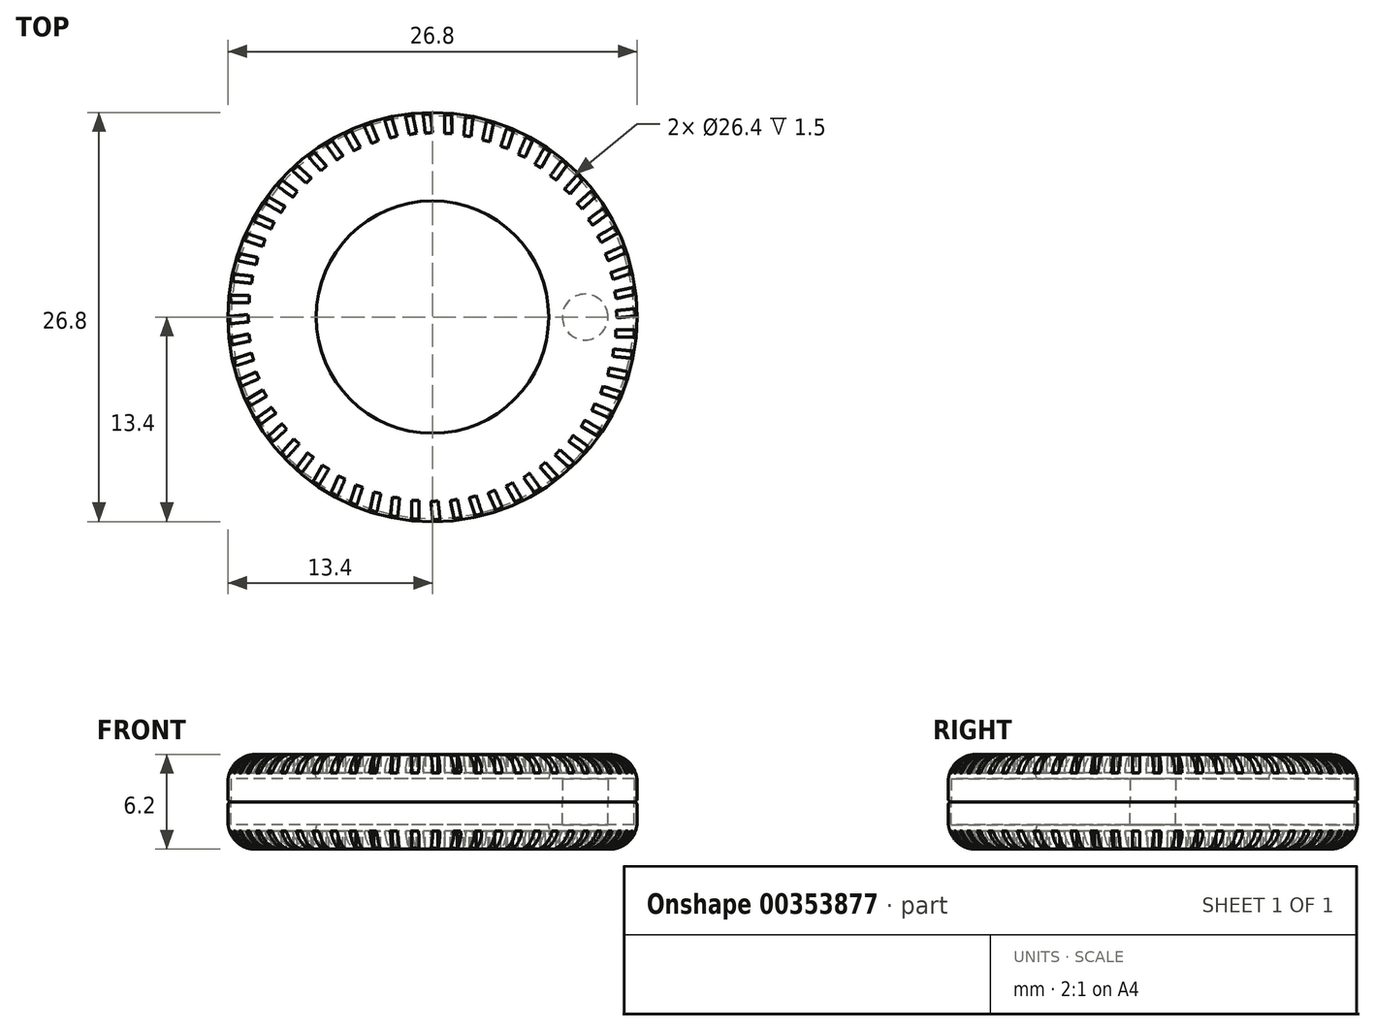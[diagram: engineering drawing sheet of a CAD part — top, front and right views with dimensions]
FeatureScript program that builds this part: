
annotation { "Feature Type Name" : "Feature", "Feature Type Description" : "" }
export const myFeature = defineFeature(function(context is Context, id is Id, definition is map)
    precondition{}
    {
        {
            var Q0;
            Q0=qCreatedBy(makeId("Top.planeOp"),FACE);
            var sketch = newSketch(context, id + "F0", { "sketchPlane" : qUnion([Q0])});
            skCircle(sketch, "E0", {"center": v(0, 0) * mm, "radius": 13.4 * mm});
            skCircle(sketch, "E1", {"center": v(0, 0) * mm, "radius": 7.6 * mm});
            skSolve(sketch);
        }
        {
            var Q0;
            Q0=makeQuery(id+"F0.imprint","IMPRINT",FACE,{"disambiguationData":[TD([[makeQuery(id+"F0.imprint","IMPRINT",EDGE,{"derivedFrom":sQuery(id+"F0.wireOp",EDGE,"E0")}),1.0]])]});
            extrude(context, id + "F1", {"entities" : qUnion([Q0]), "depth" : 3.1 * mm});
        }
        {
            var Q0;
            Q0=makeQuery(id+"F1.opExtrude","CAP_EDGE",EDGE,{"disambiguationData":[OSD([sQuery(id+"F0.wireOp",EDGE,"E0")])],"isStart":true});
            fillet(context, id + "F2", {"entities" : qUnion([Q0]), "radius" : .2 * mm, "tangentPropagation" : true, "allowEdgeOverflow" : false});
        }
        {
            var Q0;
            Q0=makeQuery(id+"F1.opExtrude","CAP_EDGE",EDGE,{"disambiguationData":[OSD([sQuery(id+"F0.wireOp",EDGE,"E0")])],"isStart":false});
            var Q1;
            Q1=makeQuery(id+"F1.opExtrude","CAP_EDGE",EDGE,{"disambiguationData":[OSD([sQuery(id+"F0.wireOp",EDGE,"E1")])],"isStart":false});
            fillet(context, id + "F3", {"entities" : qUnion([Q0, Q1]), "radius" : 1.8 * mm, "tangentPropagation" : true, "allowEdgeOverflow" : false});
        }
        {
            var Q0;
            Q0=qCreatedBy(makeId("Top.planeOp"),FACE);
            var sketch = newSketch(context, id + "F4", { "sketchPlane" : qUnion([Q0])});
            skLineSegment(sketch, "E2", {"start": v(0, 13.73) * mm, "end": v(-0.13, 13.18) * mm});
            skLineSegment(sketch, "E3", {"start": v(-0.13, 13.18) * mm, "end": v(0, 12.1) * mm});
            skLineSegment(sketch, "E4", {"start": v(0, 12.1) * mm, "end": v(-0.47, 12.04) * mm});
            skLineSegment(sketch, "E5", {"start": v(-0.47, 12.04) * mm, "end": v(-0.6, 13.18) * mm});
            skLineSegment(sketch, "E6", {"start": v(-0.6, 13.18) * mm, "end": v(-0.48, 13.73) * mm});
            skLineSegment(sketch, "E7", {"start": v(-0.48, 13.73) * mm, "end": v(0, 13.73) * mm});
            skLineSegment(sketch, "E8.1.0", {"start": v(1.26, 13.12) * mm, "end": v(1.27, 12.02) * mm});
            skLineSegment(sketch, "E8.1.1", {"start": v(1.44, 13.65) * mm, "end": v(1.26, 13.12) * mm});
            skLineSegment(sketch, "E8.1.2", {"start": v(0.8, 12.02) * mm, "end": v(0.78, 13.17) * mm});
            skLineSegment(sketch, "E8.1.3", {"start": v(0.78, 13.17) * mm, "end": v(0.96, 13.7) * mm});
            skLineSegment(sketch, "E8.1.4", {"start": v(1.27, 12.02) * mm, "end": v(0.8, 12.02) * mm});
            skLineSegment(sketch, "E8.1.5", {"start": v(0.96, 13.7) * mm, "end": v(1.44, 13.65) * mm});
            skLineSegment(sketch, "E8.2.0", {"start": v(2.63, 12.92) * mm, "end": v(2.52, 11.82) * mm});
            skLineSegment(sketch, "E8.2.1", {"start": v(2.86, 13.43) * mm, "end": v(2.63, 12.92) * mm});
            skLineSegment(sketch, "E8.2.2", {"start": v(2.05, 11.87) * mm, "end": v(2.16, 13.02) * mm});
            skLineSegment(sketch, "E8.2.3", {"start": v(2.16, 13.02) * mm, "end": v(2.4, 13.53) * mm});
            skLineSegment(sketch, "E8.2.4", {"start": v(2.52, 11.82) * mm, "end": v(2.05, 11.87) * mm});
            skLineSegment(sketch, "E8.2.5", {"start": v(2.4, 13.53) * mm, "end": v(2.86, 13.43) * mm});
            skLineSegment(sketch, "E8.3.0", {"start": v(3.96, 12.57) * mm, "end": v(3.75, 11.5) * mm});
            skLineSegment(sketch, "E8.3.1", {"start": v(4.25, 13.05) * mm, "end": v(3.96, 12.57) * mm});
            skLineSegment(sketch, "E8.3.2", {"start": v(3.28, 11.6) * mm, "end": v(3.51, 12.72) * mm});
            skLineSegment(sketch, "E8.3.3", {"start": v(3.51, 12.72) * mm, "end": v(3.8, 13.2) * mm});
            skLineSegment(sketch, "E8.3.4", {"start": v(3.75, 11.5) * mm, "end": v(3.28, 11.6) * mm});
            skLineSegment(sketch, "E8.3.5", {"start": v(3.8, 13.2) * mm, "end": v(4.25, 13.05) * mm});
            skLineSegment(sketch, "E8.4.0", {"start": v(5.26, 12.08) * mm, "end": v(4.93, 11.04) * mm});
            skLineSegment(sketch, "E8.4.1", {"start": v(5.6, 12.54) * mm, "end": v(5.26, 12.08) * mm});
            skLineSegment(sketch, "E8.4.2", {"start": v(4.48, 11.18) * mm, "end": v(4.82, 12.28) * mm});
            skLineSegment(sketch, "E8.4.3", {"start": v(4.82, 12.28) * mm, "end": v(5.16, 12.73) * mm});
            skLineSegment(sketch, "E8.4.4", {"start": v(4.93, 11.04) * mm, "end": v(4.48, 11.18) * mm});
            skLineSegment(sketch, "E8.4.5", {"start": v(5.16, 12.73) * mm, "end": v(5.6, 12.54) * mm});
            skLineSegment(sketch, "E8.5.0", {"start": v(6.5, 11.47) * mm, "end": v(6.06, 10.46) * mm});
            skLineSegment(sketch, "E8.5.1", {"start": v(6.88, 11.88) * mm, "end": v(6.5, 11.47) * mm});
            skLineSegment(sketch, "E8.5.2", {"start": v(5.63, 10.65) * mm, "end": v(6.08, 11.7) * mm});
            skLineSegment(sketch, "E8.5.3", {"start": v(6.08, 11.7) * mm, "end": v(6.47, 12.12) * mm});
            skLineSegment(sketch, "E8.5.4", {"start": v(6.06, 10.46) * mm, "end": v(5.63, 10.65) * mm});
            skLineSegment(sketch, "E8.5.5", {"start": v(6.47, 12.12) * mm, "end": v(6.88, 11.88) * mm});
            skLineSegment(sketch, "E8.6.0", {"start": v(7.66, 10.72) * mm, "end": v(7.12, 9.77) * mm});
            skLineSegment(sketch, "E8.6.1", {"start": v(8.09, 11.1) * mm, "end": v(7.66, 10.72) * mm});
            skLineSegment(sketch, "E8.6.2", {"start": v(6.71, 10) * mm, "end": v(7.28, 11) * mm});
            skLineSegment(sketch, "E8.6.3", {"start": v(7.28, 11) * mm, "end": v(7.7, 11.37) * mm});
            skLineSegment(sketch, "E8.6.4", {"start": v(7.12, 9.77) * mm, "end": v(6.71, 10) * mm});
            skLineSegment(sketch, "E8.6.5", {"start": v(7.7, 11.37) * mm, "end": v(8.09, 11.1) * mm});
            skLineSegment(sketch, "E8.7.0", {"start": v(8.75, 9.86) * mm, "end": v(8.1, 8.97) * mm});
            skLineSegment(sketch, "E8.7.1", {"start": v(9.2, 10.18) * mm, "end": v(8.75, 9.86) * mm});
            skLineSegment(sketch, "E8.7.2", {"start": v(7.72, 9.24) * mm, "end": v(8.4, 10.18) * mm});
            skLineSegment(sketch, "E8.7.3", {"start": v(8.4, 10.18) * mm, "end": v(8.85, 10.5) * mm});
            skLineSegment(sketch, "E8.7.4", {"start": v(8.1, 8.97) * mm, "end": v(7.72, 9.24) * mm});
            skLineSegment(sketch, "E8.7.5", {"start": v(8.85, 10.5) * mm, "end": v(9.2, 10.18) * mm});
            skLineSegment(sketch, "E8.8.0", {"start": v(9.73, 8.89) * mm, "end": v(9, 8.07) * mm});
            skLineSegment(sketch, "E8.8.1", {"start": v(10.22, 9.16) * mm, "end": v(9.73, 8.89) * mm});
            skLineSegment(sketch, "E8.8.2", {"start": v(8.65, 8.38) * mm, "end": v(9.41, 9.24) * mm});
            skLineSegment(sketch, "E8.8.3", {"start": v(9.41, 9.24) * mm, "end": v(9.9, 9.52) * mm});
            skLineSegment(sketch, "E8.8.4", {"start": v(9, 8.07) * mm, "end": v(8.65, 8.38) * mm});
            skLineSegment(sketch, "E8.8.5", {"start": v(9.9, 9.52) * mm, "end": v(10.22, 9.16) * mm});
            skLineSegment(sketch, "E8.9.0", {"start": v(10.6, 7.82) * mm, "end": v(9.8, 7.08) * mm});
            skLineSegment(sketch, "E8.9.1", {"start": v(11.13, 8.04) * mm, "end": v(10.6, 7.82) * mm});
            skLineSegment(sketch, "E8.9.2", {"start": v(9.48, 7.43) * mm, "end": v(10.33, 8.2) * mm});
            skLineSegment(sketch, "E8.9.3", {"start": v(10.33, 8.2) * mm, "end": v(10.85, 8.43) * mm});
            skLineSegment(sketch, "E8.9.4", {"start": v(9.8, 7.08) * mm, "end": v(9.48, 7.43) * mm});
            skLineSegment(sketch, "E8.9.5", {"start": v(10.85, 8.43) * mm, "end": v(11.13, 8.04) * mm});
            skLineSegment(sketch, "E8.10.0", {"start": v(11.37, 6.66) * mm, "end": v(10.49, 6.01) * mm});
            skLineSegment(sketch, "E8.10.1", {"start": v(11.91, 6.83) * mm, "end": v(11.37, 6.66) * mm});
            skLineSegment(sketch, "E8.10.2", {"start": v(10.2, 6.4) * mm, "end": v(11.13, 7.08) * mm});
            skLineSegment(sketch, "E8.10.3", {"start": v(11.13, 7.08) * mm, "end": v(11.67, 7.24) * mm});
            skLineSegment(sketch, "E8.10.4", {"start": v(10.49, 6.01) * mm, "end": v(10.2, 6.4) * mm});
            skLineSegment(sketch, "E8.10.5", {"start": v(11.67, 7.24) * mm, "end": v(11.91, 6.83) * mm});
            skLineSegment(sketch, "E8.11.0", {"start": v(12, 5.44) * mm, "end": v(11.06, 4.88) * mm});
            skLineSegment(sketch, "E8.11.1", {"start": v(12.56, 5.54) * mm, "end": v(12, 5.44) * mm});
            skLineSegment(sketch, "E8.11.2", {"start": v(10.82, 5.3) * mm, "end": v(11.81, 5.87) * mm});
            skLineSegment(sketch, "E8.11.3", {"start": v(11.81, 5.87) * mm, "end": v(12.37, 5.98) * mm});
            skLineSegment(sketch, "E8.11.4", {"start": v(11.06, 4.88) * mm, "end": v(10.82, 5.3) * mm});
            skLineSegment(sketch, "E8.11.5", {"start": v(12.37, 5.98) * mm, "end": v(12.56, 5.54) * mm});
            skLineSegment(sketch, "E8.12.0", {"start": v(12.51, 4.15) * mm, "end": v(11.51, 3.7) * mm});
            skLineSegment(sketch, "E8.12.1", {"start": v(13.07, 4.2) * mm, "end": v(12.51, 4.15) * mm});
            skLineSegment(sketch, "E8.12.2", {"start": v(11.32, 4.13) * mm, "end": v(12.36, 4.6) * mm});
            skLineSegment(sketch, "E8.12.3", {"start": v(12.36, 4.6) * mm, "end": v(12.93, 4.65) * mm});
            skLineSegment(sketch, "E8.12.4", {"start": v(11.51, 3.7) * mm, "end": v(11.32, 4.13) * mm});
            skLineSegment(sketch, "E8.12.5", {"start": v(12.93, 4.65) * mm, "end": v(13.07, 4.2) * mm});
            skLineSegment(sketch, "E8.13.0", {"start": v(12.88, 2.81) * mm, "end": v(11.84, 2.47) * mm});
            skLineSegment(sketch, "E8.13.1", {"start": v(13.44, 2.8) * mm, "end": v(12.88, 2.81) * mm});
            skLineSegment(sketch, "E8.13.2", {"start": v(11.69, 2.92) * mm, "end": v(12.78, 3.28) * mm});
            skLineSegment(sketch, "E8.13.3", {"start": v(12.78, 3.28) * mm, "end": v(13.34, 3.27) * mm});
            skLineSegment(sketch, "E8.13.4", {"start": v(11.84, 2.47) * mm, "end": v(11.69, 2.92) * mm});
            skLineSegment(sketch, "E8.13.5", {"start": v(13.34, 3.27) * mm, "end": v(13.44, 2.8) * mm});
            skLineSegment(sketch, "E8.14.0", {"start": v(13.1, 1.45) * mm, "end": v(12.03, 1.21) * mm});
            skLineSegment(sketch, "E8.14.1", {"start": v(13.66, 1.38) * mm, "end": v(13.1, 1.45) * mm});
            skLineSegment(sketch, "E8.14.2", {"start": v(11.93, 1.68) * mm, "end": v(13.05, 1.92) * mm});
            skLineSegment(sketch, "E8.14.3", {"start": v(13.05, 1.92) * mm, "end": v(13.61, 1.85) * mm});
            skLineSegment(sketch, "E8.14.4", {"start": v(12.03, 1.21) * mm, "end": v(11.93, 1.68) * mm});
            skLineSegment(sketch, "E8.14.5", {"start": v(13.61, 1.85) * mm, "end": v(13.66, 1.38) * mm});
            skLineSegment(sketch, "E8.15.0", {"start": v(13.18, 0.07) * mm, "end": v(12.1, -0.05) * mm});
            skLineSegment(sketch, "E8.15.1", {"start": v(13.73, -0.06) * mm, "end": v(13.18, 0.07) * mm});
            skLineSegment(sketch, "E8.15.2", {"start": v(12.04, 0.42) * mm, "end": v(13.18, 0.54) * mm});
            skLineSegment(sketch, "E8.15.3", {"start": v(13.18, 0.54) * mm, "end": v(13.73, 0.42) * mm});
            skLineSegment(sketch, "E8.15.4", {"start": v(12.1, -0.05) * mm, "end": v(12.04, 0.42) * mm});
            skLineSegment(sketch, "E8.15.5", {"start": v(13.73, 0.42) * mm, "end": v(13.73, -0.06) * mm});
            skLineSegment(sketch, "E8.16.0", {"start": v(13.11, -1.32) * mm, "end": v(12.02, -1.32) * mm});
            skLineSegment(sketch, "E8.16.1", {"start": v(13.65, -1.5) * mm, "end": v(13.11, -1.32) * mm});
            skLineSegment(sketch, "E8.16.2", {"start": v(12.02, -0.85) * mm, "end": v(13.17, -0.84) * mm});
            skLineSegment(sketch, "E8.16.3", {"start": v(13.17, -0.84) * mm, "end": v(13.7, -1.02) * mm});
            skLineSegment(sketch, "E8.16.4", {"start": v(12.02, -1.32) * mm, "end": v(12.02, -0.85) * mm});
            skLineSegment(sketch, "E8.16.5", {"start": v(13.7, -1.02) * mm, "end": v(13.65, -1.5) * mm});
            skLineSegment(sketch, "E8.17.0", {"start": v(12.9, -2.68) * mm, "end": v(11.81, -2.57) * mm});
            skLineSegment(sketch, "E8.17.1", {"start": v(13.41, -2.92) * mm, "end": v(12.9, -2.68) * mm});
            skLineSegment(sketch, "E8.17.2", {"start": v(11.86, -2.1) * mm, "end": v(13, -2.22) * mm});
            skLineSegment(sketch, "E8.17.3", {"start": v(13, -2.22) * mm, "end": v(13.52, -2.46) * mm});
            skLineSegment(sketch, "E8.17.4", {"start": v(11.81, -2.57) * mm, "end": v(11.86, -2.1) * mm});
            skLineSegment(sketch, "E8.17.5", {"start": v(13.52, -2.46) * mm, "end": v(13.41, -2.92) * mm});
            skLineSegment(sketch, "E8.18.0", {"start": v(12.55, -4.02) * mm, "end": v(11.48, -3.8) * mm});
            skLineSegment(sketch, "E8.18.1", {"start": v(13.03, -4.31) * mm, "end": v(12.55, -4.02) * mm});
            skLineSegment(sketch, "E8.18.2", {"start": v(11.58, -3.33) * mm, "end": v(12.7, -3.57) * mm});
            skLineSegment(sketch, "E8.18.3", {"start": v(12.7, -3.57) * mm, "end": v(13.18, -3.86) * mm});
            skLineSegment(sketch, "E8.18.4", {"start": v(11.48, -3.8) * mm, "end": v(11.58, -3.33) * mm});
            skLineSegment(sketch, "E8.18.5", {"start": v(13.18, -3.86) * mm, "end": v(13.03, -4.31) * mm});
            skLineSegment(sketch, "E8.19.0", {"start": v(12.06, -5.31) * mm, "end": v(11.02, -4.98) * mm});
            skLineSegment(sketch, "E8.19.1", {"start": v(12.51, -5.65) * mm, "end": v(12.06, -5.31) * mm});
            skLineSegment(sketch, "E8.19.2", {"start": v(11.16, -4.53) * mm, "end": v(12.26, -4.88) * mm});
            skLineSegment(sketch, "E8.19.3", {"start": v(12.26, -4.88) * mm, "end": v(12.7, -5.22) * mm});
            skLineSegment(sketch, "E8.19.4", {"start": v(11.02, -4.98) * mm, "end": v(11.16, -4.53) * mm});
            skLineSegment(sketch, "E8.19.5", {"start": v(12.7, -5.22) * mm, "end": v(12.51, -5.65) * mm});
            skLineSegment(sketch, "E8.20.0", {"start": v(11.44, -6.55) * mm, "end": v(10.43, -6.1) * mm});
            skLineSegment(sketch, "E8.20.1", {"start": v(11.85, -6.93) * mm, "end": v(11.44, -6.55) * mm});
            skLineSegment(sketch, "E8.20.2", {"start": v(10.63, -5.67) * mm, "end": v(11.68, -6.14) * mm});
            skLineSegment(sketch, "E8.20.3", {"start": v(11.68, -6.14) * mm, "end": v(12.1, -6.52) * mm});
            skLineSegment(sketch, "E8.20.4", {"start": v(10.43, -6.1) * mm, "end": v(10.63, -5.67) * mm});
            skLineSegment(sketch, "E8.20.5", {"start": v(12.1, -6.52) * mm, "end": v(11.85, -6.93) * mm});
            skLineSegment(sketch, "E8.21.0", {"start": v(10.69, -7.71) * mm, "end": v(9.74, -7.17) * mm});
            skLineSegment(sketch, "E8.21.1", {"start": v(11.06, -8.14) * mm, "end": v(10.69, -7.71) * mm});
            skLineSegment(sketch, "E8.21.2", {"start": v(9.97, -6.76) * mm, "end": v(10.97, -7.33) * mm});
            skLineSegment(sketch, "E8.21.3", {"start": v(10.97, -7.33) * mm, "end": v(11.34, -7.75) * mm});
            skLineSegment(sketch, "E8.21.4", {"start": v(9.74, -7.17) * mm, "end": v(9.97, -6.76) * mm});
            skLineSegment(sketch, "E8.21.5", {"start": v(11.34, -7.75) * mm, "end": v(11.06, -8.14) * mm});
            skLineSegment(sketch, "E8.22.0", {"start": v(9.82, -8.79) * mm, "end": v(8.93, -8.15) * mm});
            skLineSegment(sketch, "E8.22.1", {"start": v(10.14, -9.25) * mm, "end": v(9.82, -8.79) * mm});
            skLineSegment(sketch, "E8.22.2", {"start": v(9.2, -7.76) * mm, "end": v(10.14, -8.44) * mm});
            skLineSegment(sketch, "E8.22.3", {"start": v(10.14, -8.44) * mm, "end": v(10.46, -8.9) * mm});
            skLineSegment(sketch, "E8.22.4", {"start": v(8.93, -8.15) * mm, "end": v(9.2, -7.76) * mm});
            skLineSegment(sketch, "E8.22.5", {"start": v(10.46, -8.9) * mm, "end": v(10.14, -9.25) * mm});
            skLineSegment(sketch, "E8.23.0", {"start": v(8.85, -9.77) * mm, "end": v(8.03, -9.04) * mm});
            skLineSegment(sketch, "E8.23.1", {"start": v(9.12, -10.27) * mm, "end": v(8.85, -9.77) * mm});
            skLineSegment(sketch, "E8.23.2", {"start": v(8.35, -8.69) * mm, "end": v(9.2, -9.45) * mm});
            skLineSegment(sketch, "E8.23.3", {"start": v(9.2, -9.45) * mm, "end": v(9.47, -9.95) * mm});
            skLineSegment(sketch, "E8.23.4", {"start": v(8.03, -9.04) * mm, "end": v(8.35, -8.69) * mm});
            skLineSegment(sketch, "E8.23.5", {"start": v(9.47, -9.95) * mm, "end": v(9.12, -10.27) * mm});
            skLineSegment(sketch, "E8.24.0", {"start": v(7.77, -10.64) * mm, "end": v(7.04, -9.83) * mm});
            skLineSegment(sketch, "E8.24.1", {"start": v(8, -11.16) * mm, "end": v(7.77, -10.64) * mm});
            skLineSegment(sketch, "E8.24.2", {"start": v(7.39, -9.51) * mm, "end": v(8.16, -10.37) * mm});
            skLineSegment(sketch, "E8.24.3", {"start": v(8.16, -10.37) * mm, "end": v(8.38, -10.89) * mm});
            skLineSegment(sketch, "E8.24.4", {"start": v(7.04, -9.83) * mm, "end": v(7.39, -9.51) * mm});
            skLineSegment(sketch, "E8.24.5", {"start": v(8.38, -10.89) * mm, "end": v(8, -11.16) * mm});
            skLineSegment(sketch, "E8.25.0", {"start": v(6.61, -11.4) * mm, "end": v(5.97, -10.52) * mm});
            skLineSegment(sketch, "E8.25.1", {"start": v(6.78, -11.94) * mm, "end": v(6.61, -11.4) * mm});
            skLineSegment(sketch, "E8.25.2", {"start": v(6.35, -10.24) * mm, "end": v(7.03, -11.16) * mm});
            skLineSegment(sketch, "E8.25.3", {"start": v(7.03, -11.16) * mm, "end": v(7.2, -11.7) * mm});
            skLineSegment(sketch, "E8.25.4", {"start": v(5.97, -10.52) * mm, "end": v(6.35, -10.24) * mm});
            skLineSegment(sketch, "E8.25.5", {"start": v(7.2, -11.7) * mm, "end": v(6.78, -11.94) * mm});
            skLineSegment(sketch, "E8.26.0", {"start": v(5.38, -12.03) * mm, "end": v(4.83, -11.08) * mm});
            skLineSegment(sketch, "E8.26.1", {"start": v(5.49, -12.58) * mm, "end": v(5.38, -12.03) * mm});
            skLineSegment(sketch, "E8.26.2", {"start": v(5.24, -10.84) * mm, "end": v(5.82, -11.84) * mm});
            skLineSegment(sketch, "E8.26.3", {"start": v(5.82, -11.84) * mm, "end": v(5.93, -12.4) * mm});
            skLineSegment(sketch, "E8.26.4", {"start": v(4.83, -11.08) * mm, "end": v(5.24, -10.84) * mm});
            skLineSegment(sketch, "E8.26.5", {"start": v(5.93, -12.4) * mm, "end": v(5.49, -12.58) * mm});
            skLineSegment(sketch, "E8.27.0", {"start": v(4.1, -12.53) * mm, "end": v(3.64, -11.53) * mm});
            skLineSegment(sketch, "E8.27.1", {"start": v(4.14, -13.1) * mm, "end": v(4.1, -12.53) * mm});
            skLineSegment(sketch, "E8.27.2", {"start": v(4.08, -11.33) * mm, "end": v(4.55, -12.38) * mm});
            skLineSegment(sketch, "E8.27.3", {"start": v(4.55, -12.38) * mm, "end": v(4.6, -12.95) * mm});
            skLineSegment(sketch, "E8.27.4", {"start": v(3.64, -11.53) * mm, "end": v(4.08, -11.33) * mm});
            skLineSegment(sketch, "E8.27.5", {"start": v(4.6, -12.95) * mm, "end": v(4.14, -13.1) * mm});
            skLineSegment(sketch, "E8.28.0", {"start": v(2.76, -12.89) * mm, "end": v(2.42, -11.85) * mm});
            skLineSegment(sketch, "E8.28.1", {"start": v(2.74, -13.45) * mm, "end": v(2.76, -12.89) * mm});
            skLineSegment(sketch, "E8.28.2", {"start": v(2.87, -11.7) * mm, "end": v(3.22, -12.8) * mm});
            skLineSegment(sketch, "E8.28.3", {"start": v(3.22, -12.8) * mm, "end": v(3.21, -13.36) * mm});
            skLineSegment(sketch, "E8.28.4", {"start": v(2.42, -11.85) * mm, "end": v(2.87, -11.7) * mm});
            skLineSegment(sketch, "E8.28.5", {"start": v(3.21, -13.36) * mm, "end": v(2.74, -13.45) * mm});
            skLineSegment(sketch, "E8.29.0", {"start": v(1.39, -13.1) * mm, "end": v(1.16, -12.03) * mm});
            skLineSegment(sketch, "E8.29.1", {"start": v(1.32, -13.67) * mm, "end": v(1.39, -13.1) * mm});
            skLineSegment(sketch, "E8.29.2", {"start": v(1.62, -11.94) * mm, "end": v(1.87, -13.06) * mm});
            skLineSegment(sketch, "E8.29.3", {"start": v(1.87, -13.06) * mm, "end": v(1.8, -13.62) * mm});
            skLineSegment(sketch, "E8.29.4", {"start": v(1.16, -12.03) * mm, "end": v(1.62, -11.94) * mm});
            skLineSegment(sketch, "E8.29.5", {"start": v(1.8, -13.62) * mm, "end": v(1.32, -13.67) * mm});
            skLineSegment(sketch, "E8.30.0", {"start": v(0, -13.18) * mm, "end": v(-0.1, -12.1) * mm});
            skLineSegment(sketch, "E8.30.1", {"start": v(-0.12, -13.73) * mm, "end": v(0, -13.18) * mm});
            skLineSegment(sketch, "E8.30.2", {"start": v(0.36, -12.04) * mm, "end": v(0.49, -13.18) * mm});
            skLineSegment(sketch, "E8.30.3", {"start": v(0.49, -13.18) * mm, "end": v(0.36, -13.73) * mm});
            skLineSegment(sketch, "E8.30.4", {"start": v(-0.1, -12.1) * mm, "end": v(0.36, -12.04) * mm});
            skLineSegment(sketch, "E8.30.5", {"start": v(0.36, -13.73) * mm, "end": v(-0.12, -13.73) * mm});
            skLineSegment(sketch, "E8.31.0", {"start": v(-1.37, -13.1) * mm, "end": v(-1.37, -12.01) * mm});
            skLineSegment(sketch, "E8.31.1", {"start": v(-1.56, -13.64) * mm, "end": v(-1.37, -13.1) * mm});
            skLineSegment(sketch, "E8.31.2", {"start": v(-0.9, -12.01) * mm, "end": v(-0.9, -13.16) * mm});
            skLineSegment(sketch, "E8.31.3", {"start": v(-0.9, -13.16) * mm, "end": v(-1.09, -13.7) * mm});
            skLineSegment(sketch, "E8.31.4", {"start": v(-1.37, -12.01) * mm, "end": v(-0.9, -12.01) * mm});
            skLineSegment(sketch, "E8.31.5", {"start": v(-1.09, -13.7) * mm, "end": v(-1.56, -13.64) * mm});
            skLineSegment(sketch, "E8.32.0", {"start": v(-2.74, -12.9) * mm, "end": v(-2.63, -11.8) * mm});
            skLineSegment(sketch, "E8.32.1", {"start": v(-2.98, -13.4) * mm, "end": v(-2.74, -12.9) * mm});
            skLineSegment(sketch, "E8.32.2", {"start": v(-2.15, -11.85) * mm, "end": v(-2.27, -13) * mm});
            skLineSegment(sketch, "E8.32.3", {"start": v(-2.27, -13) * mm, "end": v(-2.52, -13.5) * mm});
            skLineSegment(sketch, "E8.32.4", {"start": v(-2.63, -11.8) * mm, "end": v(-2.15, -11.85) * mm});
            skLineSegment(sketch, "E8.32.5", {"start": v(-2.52, -13.5) * mm, "end": v(-2.98, -13.4) * mm});
            skLineSegment(sketch, "E8.33.0", {"start": v(-4.08, -12.53) * mm, "end": v(-3.85, -11.46) * mm});
            skLineSegment(sketch, "E8.33.1", {"start": v(-4.37, -13.02) * mm, "end": v(-4.08, -12.53) * mm});
            skLineSegment(sketch, "E8.33.2", {"start": v(-3.38, -11.56) * mm, "end": v(-3.62, -12.69) * mm});
            skLineSegment(sketch, "E8.33.3", {"start": v(-3.62, -12.69) * mm, "end": v(-3.92, -13.17) * mm});
            skLineSegment(sketch, "E8.33.4", {"start": v(-3.85, -11.46) * mm, "end": v(-3.38, -11.56) * mm});
            skLineSegment(sketch, "E8.33.5", {"start": v(-3.92, -13.17) * mm, "end": v(-4.37, -13.02) * mm});
            skLineSegment(sketch, "E8.34.0", {"start": v(-5.37, -12.04) * mm, "end": v(-5.03, -11) * mm});
            skLineSegment(sketch, "E8.34.1", {"start": v(-5.71, -12.49) * mm, "end": v(-5.37, -12.04) * mm});
            skLineSegment(sketch, "E8.34.2", {"start": v(-4.58, -11.14) * mm, "end": v(-4.93, -12.24) * mm});
            skLineSegment(sketch, "E8.34.3", {"start": v(-4.93, -12.24) * mm, "end": v(-5.28, -12.68) * mm});
            skLineSegment(sketch, "E8.34.4", {"start": v(-5.03, -11) * mm, "end": v(-4.58, -11.14) * mm});
            skLineSegment(sketch, "E8.34.5", {"start": v(-5.28, -12.68) * mm, "end": v(-5.71, -12.49) * mm});
            skLineSegment(sketch, "E8.35.0", {"start": v(-6.6, -11.4) * mm, "end": v(-6.15, -10.4) * mm});
            skLineSegment(sketch, "E8.35.1", {"start": v(-6.99, -11.82) * mm, "end": v(-6.6, -11.4) * mm});
            skLineSegment(sketch, "E8.35.2", {"start": v(-5.72, -10.6) * mm, "end": v(-6.19, -11.65) * mm});
            skLineSegment(sketch, "E8.35.3", {"start": v(-6.19, -11.65) * mm, "end": v(-6.58, -12.06) * mm});
            skLineSegment(sketch, "E8.35.4", {"start": v(-6.15, -10.4) * mm, "end": v(-5.72, -10.6) * mm});
            skLineSegment(sketch, "E8.35.5", {"start": v(-6.58, -12.06) * mm, "end": v(-6.99, -11.82) * mm});
            skLineSegment(sketch, "E8.36.0", {"start": v(-7.76, -10.65) * mm, "end": v(-7.21, -9.7) * mm});
            skLineSegment(sketch, "E8.36.1", {"start": v(-8.19, -11.02) * mm, "end": v(-7.76, -10.65) * mm});
            skLineSegment(sketch, "E8.36.2", {"start": v(-6.8, -9.94) * mm, "end": v(-7.38, -10.94) * mm});
            skLineSegment(sketch, "E8.36.3", {"start": v(-7.38, -10.94) * mm, "end": v(-7.8, -11.3) * mm});
            skLineSegment(sketch, "E8.36.4", {"start": v(-7.21, -9.7) * mm, "end": v(-6.8, -9.94) * mm});
            skLineSegment(sketch, "E8.36.5", {"start": v(-7.8, -11.3) * mm, "end": v(-8.19, -11.02) * mm});
            skLineSegment(sketch, "E8.37.0", {"start": v(-8.83, -9.78) * mm, "end": v(-8.19, -8.9) * mm});
            skLineSegment(sketch, "E8.37.1", {"start": v(-9.3, -10.1) * mm, "end": v(-8.83, -9.78) * mm});
            skLineSegment(sketch, "E8.37.2", {"start": v(-7.8, -9.18) * mm, "end": v(-8.48, -10.1) * mm});
            skLineSegment(sketch, "E8.37.3", {"start": v(-8.48, -10.1) * mm, "end": v(-8.95, -10.43) * mm});
            skLineSegment(sketch, "E8.37.4", {"start": v(-8.19, -8.9) * mm, "end": v(-7.8, -9.18) * mm});
            skLineSegment(sketch, "E8.37.5", {"start": v(-8.95, -10.43) * mm, "end": v(-9.3, -10.1) * mm});
            skLineSegment(sketch, "E8.38.0", {"start": v(-9.8, -8.8) * mm, "end": v(-9.08, -7.99) * mm});
            skLineSegment(sketch, "E8.38.1", {"start": v(-10.3, -9.07) * mm, "end": v(-9.8, -8.8) * mm});
            skLineSegment(sketch, "E8.38.2", {"start": v(-8.72, -8.3) * mm, "end": v(-9.5, -9.16) * mm});
            skLineSegment(sketch, "E8.38.3", {"start": v(-9.5, -9.16) * mm, "end": v(-9.99, -9.43) * mm});
            skLineSegment(sketch, "E8.38.4", {"start": v(-9.08, -7.99) * mm, "end": v(-8.72, -8.3) * mm});
            skLineSegment(sketch, "E8.38.5", {"start": v(-9.99, -9.43) * mm, "end": v(-10.3, -9.07) * mm});
            skLineSegment(sketch, "E8.39.0", {"start": v(-10.68, -7.73) * mm, "end": v(-9.86, -7) * mm});
            skLineSegment(sketch, "E8.39.1", {"start": v(-11.2, -7.94) * mm, "end": v(-10.68, -7.73) * mm});
            skLineSegment(sketch, "E8.39.2", {"start": v(-9.55, -7.35) * mm, "end": v(-10.4, -8.11) * mm});
            skLineSegment(sketch, "E8.39.3", {"start": v(-10.4, -8.11) * mm, "end": v(-10.92, -8.33) * mm});
            skLineSegment(sketch, "E8.39.4", {"start": v(-9.86, -7) * mm, "end": v(-9.55, -7.35) * mm});
            skLineSegment(sketch, "E8.39.5", {"start": v(-10.92, -8.33) * mm, "end": v(-11.2, -7.94) * mm});
            skLineSegment(sketch, "E8.40.0", {"start": v(-11.43, -6.56) * mm, "end": v(-10.54, -5.92) * mm});
            skLineSegment(sketch, "E8.40.1", {"start": v(-11.97, -6.72) * mm, "end": v(-11.43, -6.56) * mm});
            skLineSegment(sketch, "E8.40.2", {"start": v(-10.26, -6.3) * mm, "end": v(-11.2, -6.98) * mm});
            skLineSegment(sketch, "E8.40.3", {"start": v(-11.2, -6.98) * mm, "end": v(-11.74, -7.14) * mm});
            skLineSegment(sketch, "E8.40.4", {"start": v(-10.54, -5.92) * mm, "end": v(-10.26, -6.3) * mm});
            skLineSegment(sketch, "E8.40.5", {"start": v(-11.74, -7.14) * mm, "end": v(-11.97, -6.72) * mm});
            skLineSegment(sketch, "E8.41.0", {"start": v(-12.05, -5.33) * mm, "end": v(-11.1, -4.78) * mm});
            skLineSegment(sketch, "E8.41.1", {"start": v(-12.6, -5.43) * mm, "end": v(-12.05, -5.33) * mm});
            skLineSegment(sketch, "E8.41.2", {"start": v(-10.87, -5.2) * mm, "end": v(-11.87, -5.77) * mm});
            skLineSegment(sketch, "E8.41.3", {"start": v(-11.87, -5.77) * mm, "end": v(-12.42, -5.87) * mm});
            skLineSegment(sketch, "E8.41.4", {"start": v(-11.1, -4.78) * mm, "end": v(-10.87, -5.2) * mm});
            skLineSegment(sketch, "E8.41.5", {"start": v(-12.42, -5.87) * mm, "end": v(-12.6, -5.43) * mm});
            skLineSegment(sketch, "E8.42.0", {"start": v(-12.55, -4.04) * mm, "end": v(-11.54, -3.6) * mm});
            skLineSegment(sketch, "E8.42.1", {"start": v(-13.1, -4.08) * mm, "end": v(-12.55, -4.04) * mm});
            skLineSegment(sketch, "E8.42.2", {"start": v(-11.35, -4.03) * mm, "end": v(-12.4, -4.5) * mm});
            skLineSegment(sketch, "E8.42.3", {"start": v(-12.4, -4.5) * mm, "end": v(-12.97, -4.54) * mm});
            skLineSegment(sketch, "E8.42.4", {"start": v(-11.54, -3.6) * mm, "end": v(-11.35, -4.03) * mm});
            skLineSegment(sketch, "E8.42.5", {"start": v(-12.97, -4.54) * mm, "end": v(-13.1, -4.08) * mm});
            skLineSegment(sketch, "E8.43.0", {"start": v(-12.9, -2.7) * mm, "end": v(-11.86, -2.36) * mm});
            skLineSegment(sketch, "E8.43.1", {"start": v(-13.46, -2.68) * mm, "end": v(-12.9, -2.7) * mm});
            skLineSegment(sketch, "E8.43.2", {"start": v(-11.71, -2.82) * mm, "end": v(-12.8, -3.17) * mm});
            skLineSegment(sketch, "E8.43.3", {"start": v(-12.8, -3.17) * mm, "end": v(-13.37, -3.15) * mm});
            skLineSegment(sketch, "E8.43.4", {"start": v(-11.86, -2.36) * mm, "end": v(-11.71, -2.82) * mm});
            skLineSegment(sketch, "E8.43.5", {"start": v(-13.37, -3.15) * mm, "end": v(-13.46, -2.68) * mm});
            skLineSegment(sketch, "E8.44.0", {"start": v(-13.11, -1.33) * mm, "end": v(-12.04, -1.1) * mm});
            skLineSegment(sketch, "E8.44.1", {"start": v(-13.67, -1.26) * mm, "end": v(-13.11, -1.33) * mm});
            skLineSegment(sketch, "E8.44.2", {"start": v(-11.94, -1.57) * mm, "end": v(-13.07, -1.8) * mm});
            skLineSegment(sketch, "E8.44.3", {"start": v(-13.07, -1.8) * mm, "end": v(-13.63, -1.73) * mm});
            skLineSegment(sketch, "E8.44.4", {"start": v(-12.04, -1.1) * mm, "end": v(-11.94, -1.57) * mm});
            skLineSegment(sketch, "E8.44.5", {"start": v(-13.63, -1.73) * mm, "end": v(-13.67, -1.26) * mm});
            skLineSegment(sketch, "E8.45.0", {"start": v(-13.18, 0.05) * mm, "end": v(-12.09, 0.16) * mm});
            skLineSegment(sketch, "E8.45.1", {"start": v(-13.73, 0.18) * mm, "end": v(-13.18, 0.05) * mm});
            skLineSegment(sketch, "E8.45.2", {"start": v(-12.04, -0.31) * mm, "end": v(-13.19, -0.43) * mm});
            skLineSegment(sketch, "E8.45.3", {"start": v(-13.19, -0.43) * mm, "end": v(-13.73, -0.3) * mm});
            skLineSegment(sketch, "E8.45.4", {"start": v(-12.09, 0.16) * mm, "end": v(-12.04, -0.31) * mm});
            skLineSegment(sketch, "E8.45.5", {"start": v(-13.73, -0.3) * mm, "end": v(-13.73, 0.18) * mm});
            skLineSegment(sketch, "E8.46.0", {"start": v(-13.1, 1.43) * mm, "end": v(-12, 1.43) * mm});
            skLineSegment(sketch, "E8.46.1", {"start": v(-13.63, 1.62) * mm, "end": v(-13.1, 1.43) * mm});
            skLineSegment(sketch, "E8.46.2", {"start": v(-12, 0.95) * mm, "end": v(-13.16, 0.96) * mm});
            skLineSegment(sketch, "E8.46.3", {"start": v(-13.16, 0.96) * mm, "end": v(-13.69, 1.15) * mm});
            skLineSegment(sketch, "E8.46.4", {"start": v(-12, 1.43) * mm, "end": v(-12, 0.95) * mm});
            skLineSegment(sketch, "E8.46.5", {"start": v(-13.69, 1.15) * mm, "end": v(-13.63, 1.62) * mm});
            skLineSegment(sketch, "E8.47.0", {"start": v(-12.88, 2.8) * mm, "end": v(-11.8, 2.68) * mm});
            skLineSegment(sketch, "E8.47.1", {"start": v(-13.39, 3.04) * mm, "end": v(-12.88, 2.8) * mm});
            skLineSegment(sketch, "E8.47.2", {"start": v(-11.84, 2.2) * mm, "end": v(-12.99, 2.33) * mm});
            skLineSegment(sketch, "E8.47.3", {"start": v(-12.99, 2.33) * mm, "end": v(-13.5, 2.57) * mm});
            skLineSegment(sketch, "E8.47.4", {"start": v(-11.8, 2.68) * mm, "end": v(-11.84, 2.2) * mm});
            skLineSegment(sketch, "E8.47.5", {"start": v(-13.5, 2.57) * mm, "end": v(-13.39, 3.04) * mm});
            skLineSegment(sketch, "E8.48.0", {"start": v(-12.52, 4.13) * mm, "end": v(-11.44, 3.9) * mm});
            skLineSegment(sketch, "E8.48.1", {"start": v(-13, 4.43) * mm, "end": v(-12.52, 4.13) * mm});
            skLineSegment(sketch, "E8.48.2", {"start": v(-11.55, 3.44) * mm, "end": v(-12.67, 3.68) * mm});
            skLineSegment(sketch, "E8.48.3", {"start": v(-12.67, 3.68) * mm, "end": v(-13.15, 3.98) * mm});
            skLineSegment(sketch, "E8.48.4", {"start": v(-11.44, 3.9) * mm, "end": v(-11.55, 3.44) * mm});
            skLineSegment(sketch, "E8.48.5", {"start": v(-13.15, 3.98) * mm, "end": v(-13, 4.43) * mm});
            skLineSegment(sketch, "E8.49.0", {"start": v(-12.01, 5.42) * mm, "end": v(-10.97, 5.08) * mm});
            skLineSegment(sketch, "E8.49.1", {"start": v(-12.46, 5.77) * mm, "end": v(-12.01, 5.42) * mm});
            skLineSegment(sketch, "E8.49.2", {"start": v(-11.12, 4.63) * mm, "end": v(-12.21, 4.99) * mm});
            skLineSegment(sketch, "E8.49.3", {"start": v(-12.21, 4.99) * mm, "end": v(-12.66, 5.33) * mm});
            skLineSegment(sketch, "E8.49.4", {"start": v(-10.97, 5.08) * mm, "end": v(-11.12, 4.63) * mm});
            skLineSegment(sketch, "E8.49.5", {"start": v(-12.66, 5.33) * mm, "end": v(-12.46, 5.77) * mm});
            skLineSegment(sketch, "E8.50.0", {"start": v(-11.38, 6.65) * mm, "end": v(-10.38, 6.2) * mm});
            skLineSegment(sketch, "E8.50.1", {"start": v(-11.79, 7.04) * mm, "end": v(-11.38, 6.65) * mm});
            skLineSegment(sketch, "E8.50.2", {"start": v(-10.58, 5.77) * mm, "end": v(-11.62, 6.24) * mm});
            skLineSegment(sketch, "E8.50.3", {"start": v(-11.62, 6.24) * mm, "end": v(-12.03, 6.63) * mm});
            skLineSegment(sketch, "E8.50.4", {"start": v(-10.38, 6.2) * mm, "end": v(-10.58, 5.77) * mm});
            skLineSegment(sketch, "E8.50.5", {"start": v(-12.03, 6.63) * mm, "end": v(-11.79, 7.04) * mm});
            skLineSegment(sketch, "E8.51.0", {"start": v(-10.62, 7.8) * mm, "end": v(-9.67, 7.25) * mm});
            skLineSegment(sketch, "E8.51.1", {"start": v(-10.98, 8.24) * mm, "end": v(-10.62, 7.8) * mm});
            skLineSegment(sketch, "E8.51.2", {"start": v(-9.91, 6.84) * mm, "end": v(-10.9, 7.42) * mm});
            skLineSegment(sketch, "E8.51.3", {"start": v(-10.9, 7.42) * mm, "end": v(-11.27, 7.85) * mm});
            skLineSegment(sketch, "E8.51.4", {"start": v(-9.67, 7.25) * mm, "end": v(-9.91, 6.84) * mm});
            skLineSegment(sketch, "E8.51.5", {"start": v(-11.27, 7.85) * mm, "end": v(-10.98, 8.24) * mm});
            skLineSegment(sketch, "E8.52.0", {"start": v(-9.74, 8.88) * mm, "end": v(-8.86, 8.23) * mm});
            skLineSegment(sketch, "E8.52.1", {"start": v(-10.06, 9.34) * mm, "end": v(-9.74, 8.88) * mm});
            skLineSegment(sketch, "E8.52.2", {"start": v(-9.14, 7.84) * mm, "end": v(-10.07, 8.53) * mm});
            skLineSegment(sketch, "E8.52.3", {"start": v(-10.07, 8.53) * mm, "end": v(-10.39, 9) * mm});
            skLineSegment(sketch, "E8.52.4", {"start": v(-8.86, 8.23) * mm, "end": v(-9.14, 7.84) * mm});
            skLineSegment(sketch, "E8.52.5", {"start": v(-10.39, 9) * mm, "end": v(-10.06, 9.34) * mm});
            skLineSegment(sketch, "E8.53.0", {"start": v(-8.76, 9.85) * mm, "end": v(-7.95, 9.11) * mm});
            skLineSegment(sketch, "E8.53.1", {"start": v(-9.03, 10.35) * mm, "end": v(-8.76, 9.85) * mm});
            skLineSegment(sketch, "E8.53.2", {"start": v(-8.27, 8.76) * mm, "end": v(-9.12, 9.53) * mm});
            skLineSegment(sketch, "E8.53.3", {"start": v(-9.12, 9.53) * mm, "end": v(-9.39, 10.03) * mm});
            skLineSegment(sketch, "E8.53.4", {"start": v(-7.95, 9.11) * mm, "end": v(-8.27, 8.76) * mm});
            skLineSegment(sketch, "E8.53.5", {"start": v(-9.39, 10.03) * mm, "end": v(-9.03, 10.35) * mm});
            skLineSegment(sketch, "E8.54.0", {"start": v(-7.68, 10.71) * mm, "end": v(-6.95, 9.9) * mm});
            skLineSegment(sketch, "E8.54.1", {"start": v(-7.9, 11.23) * mm, "end": v(-7.68, 10.71) * mm});
            skLineSegment(sketch, "E8.54.2", {"start": v(-7.3, 9.58) * mm, "end": v(-8.07, 10.44) * mm});
            skLineSegment(sketch, "E8.54.3", {"start": v(-8.07, 10.44) * mm, "end": v(-8.28, 10.96) * mm});
            skLineSegment(sketch, "E8.54.4", {"start": v(-6.95, 9.9) * mm, "end": v(-7.3, 9.58) * mm});
            skLineSegment(sketch, "E8.54.5", {"start": v(-8.28, 10.96) * mm, "end": v(-7.9, 11.23) * mm});
            skLineSegment(sketch, "E8.55.0", {"start": v(-6.51, 11.46) * mm, "end": v(-5.87, 10.57) * mm});
            skLineSegment(sketch, "E8.55.1", {"start": v(-6.67, 12) * mm, "end": v(-6.51, 11.46) * mm});
            skLineSegment(sketch, "E8.55.2", {"start": v(-6.26, 10.3) * mm, "end": v(-6.93, 11.23) * mm});
            skLineSegment(sketch, "E8.55.3", {"start": v(-6.93, 11.23) * mm, "end": v(-7.09, 11.77) * mm});
            skLineSegment(sketch, "E8.55.4", {"start": v(-5.87, 10.57) * mm, "end": v(-6.26, 10.3) * mm});
            skLineSegment(sketch, "E8.55.5", {"start": v(-7.09, 11.77) * mm, "end": v(-6.67, 12) * mm});
            skLineSegment(sketch, "E8.56.0", {"start": v(-5.28, 12.08) * mm, "end": v(-4.73, 11.13) * mm});
            skLineSegment(sketch, "E8.56.1", {"start": v(-5.38, 12.63) * mm, "end": v(-5.28, 12.08) * mm});
            skLineSegment(sketch, "E8.56.2", {"start": v(-5.15, 10.9) * mm, "end": v(-5.72, 11.9) * mm});
            skLineSegment(sketch, "E8.56.3", {"start": v(-5.72, 11.9) * mm, "end": v(-5.82, 12.45) * mm});
            skLineSegment(sketch, "E8.56.4", {"start": v(-4.73, 11.13) * mm, "end": v(-5.15, 10.9) * mm});
            skLineSegment(sketch, "E8.56.5", {"start": v(-5.82, 12.45) * mm, "end": v(-5.38, 12.63) * mm});
            skLineSegment(sketch, "E8.57.0", {"start": v(-3.98, 12.56) * mm, "end": v(-3.54, 11.56) * mm});
            skLineSegment(sketch, "E8.57.1", {"start": v(-4.02, 13.13) * mm, "end": v(-3.98, 12.56) * mm});
            skLineSegment(sketch, "E8.57.2", {"start": v(-3.98, 11.37) * mm, "end": v(-4.44, 12.42) * mm});
            skLineSegment(sketch, "E8.57.3", {"start": v(-4.44, 12.42) * mm, "end": v(-4.48, 12.99) * mm});
            skLineSegment(sketch, "E8.57.4", {"start": v(-3.54, 11.56) * mm, "end": v(-3.98, 11.37) * mm});
            skLineSegment(sketch, "E8.57.5", {"start": v(-4.48, 12.99) * mm, "end": v(-4.02, 13.13) * mm});
            skLineSegment(sketch, "E8.58.0", {"start": v(-2.64, 12.91) * mm, "end": v(-2.31, 11.87) * mm});
            skLineSegment(sketch, "E8.58.1", {"start": v(-2.62, 13.48) * mm, "end": v(-2.64, 12.91) * mm});
            skLineSegment(sketch, "E8.58.2", {"start": v(-2.76, 11.72) * mm, "end": v(-3.11, 12.82) * mm});
            skLineSegment(sketch, "E8.58.3", {"start": v(-3.11, 12.82) * mm, "end": v(-3.1, 13.38) * mm});
            skLineSegment(sketch, "E8.58.4", {"start": v(-2.31, 11.87) * mm, "end": v(-2.76, 11.72) * mm});
            skLineSegment(sketch, "E8.58.5", {"start": v(-3.1, 13.38) * mm, "end": v(-2.62, 13.48) * mm});
            skLineSegment(sketch, "E8.59.0", {"start": v(-1.27, 13.12) * mm, "end": v(-1.05, 12.04) * mm});
            skLineSegment(sketch, "E8.59.1", {"start": v(-1.2, 13.68) * mm, "end": v(-1.27, 13.12) * mm});
            skLineSegment(sketch, "E8.59.2", {"start": v(-1.52, 11.95) * mm, "end": v(-1.75, 13.08) * mm});
            skLineSegment(sketch, "E8.59.3", {"start": v(-1.75, 13.08) * mm, "end": v(-1.67, 13.64) * mm});
            skLineSegment(sketch, "E8.59.4", {"start": v(-1.05, 12.04) * mm, "end": v(-1.52, 11.95) * mm});
            skLineSegment(sketch, "E8.59.5", {"start": v(-1.67, 13.64) * mm, "end": v(-1.2, 13.68) * mm});
            skPoint(sketch, "E8.center", {"position": v(0, 0) * mm});
            skLineSegment(sketch, "E8.anchor1", {"start": v(0, 0) * mm, "end": v(-0.47, 12.04) * mm, "construction": true});
            skLineSegment(sketch, "E8.anchor2", {"start": v(0, 0) * mm, "end": v(-1.52, 11.95) * mm, "construction": true});
            skSolve(sketch);
        }
        {
            var Q0;
            Q0 = qSketchRegion(id + "F4", true);
            extrude(context, id + "F5", {"entities" : qUnion([Q0]), "depth" : 2 * mm});
        }
        {
            var Q0;
            Q0=makeQuery(id+"F5.opExtrude","SWEPT_BODY",BODY,{"disambiguationData":[OSD([sQuery(id+"F4.wireOp",EDGE,"E2"),sQuery(id+"F4.wireOp",EDGE,"E3"),sQuery(id+"F4.wireOp",EDGE,"E4"),sQuery(id+"F4.wireOp",EDGE,"E5"),sQuery(id+"F4.wireOp",EDGE,"E6"),sQuery(id+"F4.wireOp",EDGE,"E7")])]});
            var Q1;
            Q1=makeQuery(id+"F5.opExtrude","SWEPT_BODY",BODY,{"disambiguationData":[OSD([sQuery(id+"F4.wireOp",EDGE,"E8.1.0"),sQuery(id+"F4.wireOp",EDGE,"E8.1.1"),sQuery(id+"F4.wireOp",EDGE,"E8.1.2"),sQuery(id+"F4.wireOp",EDGE,"E8.1.3"),sQuery(id+"F4.wireOp",EDGE,"E8.1.4"),sQuery(id+"F4.wireOp",EDGE,"E8.1.5")])]});
            var Q2;
            Q2=makeQuery(id+"F5.opExtrude","SWEPT_BODY",BODY,{"disambiguationData":[OSD([sQuery(id+"F4.wireOp",EDGE,"E8.2.0"),sQuery(id+"F4.wireOp",EDGE,"E8.2.1"),sQuery(id+"F4.wireOp",EDGE,"E8.2.2"),sQuery(id+"F4.wireOp",EDGE,"E8.2.3"),sQuery(id+"F4.wireOp",EDGE,"E8.2.4"),sQuery(id+"F4.wireOp",EDGE,"E8.2.5")])]});
            var Q3;
            Q3=makeQuery(id+"F5.opExtrude","SWEPT_BODY",BODY,{"disambiguationData":[OSD([sQuery(id+"F4.wireOp",EDGE,"E8.3.0"),sQuery(id+"F4.wireOp",EDGE,"E8.3.1"),sQuery(id+"F4.wireOp",EDGE,"E8.3.2"),sQuery(id+"F4.wireOp",EDGE,"E8.3.3"),sQuery(id+"F4.wireOp",EDGE,"E8.3.4"),sQuery(id+"F4.wireOp",EDGE,"E8.3.5")])]});
            var Q4;
            Q4=makeQuery(id+"F5.opExtrude","SWEPT_BODY",BODY,{"disambiguationData":[OSD([sQuery(id+"F4.wireOp",EDGE,"E8.4.0"),sQuery(id+"F4.wireOp",EDGE,"E8.4.1"),sQuery(id+"F4.wireOp",EDGE,"E8.4.2"),sQuery(id+"F4.wireOp",EDGE,"E8.4.3"),sQuery(id+"F4.wireOp",EDGE,"E8.4.4"),sQuery(id+"F4.wireOp",EDGE,"E8.4.5")])]});
            var Q5;
            Q5=makeQuery(id+"F5.opExtrude","SWEPT_BODY",BODY,{"disambiguationData":[OSD([sQuery(id+"F4.wireOp",EDGE,"E8.5.0"),sQuery(id+"F4.wireOp",EDGE,"E8.5.1"),sQuery(id+"F4.wireOp",EDGE,"E8.5.2"),sQuery(id+"F4.wireOp",EDGE,"E8.5.3"),sQuery(id+"F4.wireOp",EDGE,"E8.5.4"),sQuery(id+"F4.wireOp",EDGE,"E8.5.5")])]});
            var Q6;
            Q6=makeQuery(id+"F5.opExtrude","SWEPT_BODY",BODY,{"disambiguationData":[OSD([sQuery(id+"F4.wireOp",EDGE,"E8.6.0"),sQuery(id+"F4.wireOp",EDGE,"E8.6.1"),sQuery(id+"F4.wireOp",EDGE,"E8.6.2"),sQuery(id+"F4.wireOp",EDGE,"E8.6.3"),sQuery(id+"F4.wireOp",EDGE,"E8.6.4"),sQuery(id+"F4.wireOp",EDGE,"E8.6.5")])]});
            var Q7;
            Q7=makeQuery(id+"F5.opExtrude","SWEPT_BODY",BODY,{"disambiguationData":[OSD([sQuery(id+"F4.wireOp",EDGE,"E8.7.0"),sQuery(id+"F4.wireOp",EDGE,"E8.7.1"),sQuery(id+"F4.wireOp",EDGE,"E8.7.2"),sQuery(id+"F4.wireOp",EDGE,"E8.7.3"),sQuery(id+"F4.wireOp",EDGE,"E8.7.4"),sQuery(id+"F4.wireOp",EDGE,"E8.7.5")])]});
            var Q8;
            Q8=makeQuery(id+"F5.opExtrude","SWEPT_BODY",BODY,{"disambiguationData":[OSD([sQuery(id+"F4.wireOp",EDGE,"E8.8.0"),sQuery(id+"F4.wireOp",EDGE,"E8.8.1"),sQuery(id+"F4.wireOp",EDGE,"E8.8.2"),sQuery(id+"F4.wireOp",EDGE,"E8.8.3"),sQuery(id+"F4.wireOp",EDGE,"E8.8.4"),sQuery(id+"F4.wireOp",EDGE,"E8.8.5")])]});
            var Q9;
            Q9=makeQuery(id+"F5.opExtrude","SWEPT_BODY",BODY,{"disambiguationData":[OSD([sQuery(id+"F4.wireOp",EDGE,"E8.9.0"),sQuery(id+"F4.wireOp",EDGE,"E8.9.1"),sQuery(id+"F4.wireOp",EDGE,"E8.9.2"),sQuery(id+"F4.wireOp",EDGE,"E8.9.3"),sQuery(id+"F4.wireOp",EDGE,"E8.9.4"),sQuery(id+"F4.wireOp",EDGE,"E8.9.5")])]});
            var Q10;
            Q10=makeQuery(id+"F5.opExtrude","SWEPT_BODY",BODY,{"disambiguationData":[OSD([sQuery(id+"F4.wireOp",EDGE,"E8.10.0"),sQuery(id+"F4.wireOp",EDGE,"E8.10.1"),sQuery(id+"F4.wireOp",EDGE,"E8.10.2"),sQuery(id+"F4.wireOp",EDGE,"E8.10.3"),sQuery(id+"F4.wireOp",EDGE,"E8.10.4"),sQuery(id+"F4.wireOp",EDGE,"E8.10.5")])]});
            var Q11;
            Q11=makeQuery(id+"F5.opExtrude","SWEPT_BODY",BODY,{"disambiguationData":[OSD([sQuery(id+"F4.wireOp",EDGE,"E8.11.0"),sQuery(id+"F4.wireOp",EDGE,"E8.11.1"),sQuery(id+"F4.wireOp",EDGE,"E8.11.2"),sQuery(id+"F4.wireOp",EDGE,"E8.11.3"),sQuery(id+"F4.wireOp",EDGE,"E8.11.4"),sQuery(id+"F4.wireOp",EDGE,"E8.11.5")])]});
            var Q12;
            Q12=makeQuery(id+"F5.opExtrude","SWEPT_BODY",BODY,{"disambiguationData":[OSD([sQuery(id+"F4.wireOp",EDGE,"E8.12.0"),sQuery(id+"F4.wireOp",EDGE,"E8.12.1"),sQuery(id+"F4.wireOp",EDGE,"E8.12.2"),sQuery(id+"F4.wireOp",EDGE,"E8.12.3"),sQuery(id+"F4.wireOp",EDGE,"E8.12.4"),sQuery(id+"F4.wireOp",EDGE,"E8.12.5")])]});
            var Q13;
            Q13=makeQuery(id+"F5.opExtrude","SWEPT_BODY",BODY,{"disambiguationData":[OSD([sQuery(id+"F4.wireOp",EDGE,"E8.13.0"),sQuery(id+"F4.wireOp",EDGE,"E8.13.1"),sQuery(id+"F4.wireOp",EDGE,"E8.13.2"),sQuery(id+"F4.wireOp",EDGE,"E8.13.3"),sQuery(id+"F4.wireOp",EDGE,"E8.13.4"),sQuery(id+"F4.wireOp",EDGE,"E8.13.5")])]});
            var Q14;
            Q14=makeQuery(id+"F5.opExtrude","SWEPT_BODY",BODY,{"disambiguationData":[OSD([sQuery(id+"F4.wireOp",EDGE,"E8.14.0"),sQuery(id+"F4.wireOp",EDGE,"E8.14.1"),sQuery(id+"F4.wireOp",EDGE,"E8.14.2"),sQuery(id+"F4.wireOp",EDGE,"E8.14.3"),sQuery(id+"F4.wireOp",EDGE,"E8.14.4"),sQuery(id+"F4.wireOp",EDGE,"E8.14.5")])]});
            var Q15;
            Q15=makeQuery(id+"F5.opExtrude","SWEPT_BODY",BODY,{"disambiguationData":[OSD([sQuery(id+"F4.wireOp",EDGE,"E8.15.0"),sQuery(id+"F4.wireOp",EDGE,"E8.15.1"),sQuery(id+"F4.wireOp",EDGE,"E8.15.2"),sQuery(id+"F4.wireOp",EDGE,"E8.15.3"),sQuery(id+"F4.wireOp",EDGE,"E8.15.4"),sQuery(id+"F4.wireOp",EDGE,"E8.15.5")])]});
            var Q16;
            Q16=makeQuery(id+"F5.opExtrude","SWEPT_BODY",BODY,{"disambiguationData":[OSD([sQuery(id+"F4.wireOp",EDGE,"E8.16.0"),sQuery(id+"F4.wireOp",EDGE,"E8.16.1"),sQuery(id+"F4.wireOp",EDGE,"E8.16.2"),sQuery(id+"F4.wireOp",EDGE,"E8.16.3"),sQuery(id+"F4.wireOp",EDGE,"E8.16.4"),sQuery(id+"F4.wireOp",EDGE,"E8.16.5")])]});
            var Q17;
            Q17=makeQuery(id+"F5.opExtrude","SWEPT_BODY",BODY,{"disambiguationData":[OSD([sQuery(id+"F4.wireOp",EDGE,"E8.17.0"),sQuery(id+"F4.wireOp",EDGE,"E8.17.1"),sQuery(id+"F4.wireOp",EDGE,"E8.17.2"),sQuery(id+"F4.wireOp",EDGE,"E8.17.3"),sQuery(id+"F4.wireOp",EDGE,"E8.17.4"),sQuery(id+"F4.wireOp",EDGE,"E8.17.5")])]});
            var Q18;
            Q18=makeQuery(id+"F5.opExtrude","SWEPT_BODY",BODY,{"disambiguationData":[OSD([sQuery(id+"F4.wireOp",EDGE,"E8.18.0"),sQuery(id+"F4.wireOp",EDGE,"E8.18.1"),sQuery(id+"F4.wireOp",EDGE,"E8.18.2"),sQuery(id+"F4.wireOp",EDGE,"E8.18.3"),sQuery(id+"F4.wireOp",EDGE,"E8.18.4"),sQuery(id+"F4.wireOp",EDGE,"E8.18.5")])]});
            var Q19;
            Q19=makeQuery(id+"F5.opExtrude","SWEPT_BODY",BODY,{"disambiguationData":[OSD([sQuery(id+"F4.wireOp",EDGE,"E8.19.0"),sQuery(id+"F4.wireOp",EDGE,"E8.19.1"),sQuery(id+"F4.wireOp",EDGE,"E8.19.2"),sQuery(id+"F4.wireOp",EDGE,"E8.19.3"),sQuery(id+"F4.wireOp",EDGE,"E8.19.4"),sQuery(id+"F4.wireOp",EDGE,"E8.19.5")])]});
            var Q20;
            Q20=makeQuery(id+"F5.opExtrude","SWEPT_BODY",BODY,{"disambiguationData":[OSD([sQuery(id+"F4.wireOp",EDGE,"E8.20.0"),sQuery(id+"F4.wireOp",EDGE,"E8.20.1"),sQuery(id+"F4.wireOp",EDGE,"E8.20.2"),sQuery(id+"F4.wireOp",EDGE,"E8.20.3"),sQuery(id+"F4.wireOp",EDGE,"E8.20.4"),sQuery(id+"F4.wireOp",EDGE,"E8.20.5")])]});
            var Q21;
            Q21=makeQuery(id+"F5.opExtrude","SWEPT_BODY",BODY,{"disambiguationData":[OSD([sQuery(id+"F4.wireOp",EDGE,"E8.21.0"),sQuery(id+"F4.wireOp",EDGE,"E8.21.1"),sQuery(id+"F4.wireOp",EDGE,"E8.21.2"),sQuery(id+"F4.wireOp",EDGE,"E8.21.3"),sQuery(id+"F4.wireOp",EDGE,"E8.21.4"),sQuery(id+"F4.wireOp",EDGE,"E8.21.5")])]});
            var Q22;
            Q22=makeQuery(id+"F5.opExtrude","SWEPT_BODY",BODY,{"disambiguationData":[OSD([sQuery(id+"F4.wireOp",EDGE,"E8.22.0"),sQuery(id+"F4.wireOp",EDGE,"E8.22.1"),sQuery(id+"F4.wireOp",EDGE,"E8.22.2"),sQuery(id+"F4.wireOp",EDGE,"E8.22.3"),sQuery(id+"F4.wireOp",EDGE,"E8.22.4"),sQuery(id+"F4.wireOp",EDGE,"E8.22.5")])]});
            var Q23;
            Q23=makeQuery(id+"F5.opExtrude","SWEPT_BODY",BODY,{"disambiguationData":[OSD([sQuery(id+"F4.wireOp",EDGE,"E8.23.0"),sQuery(id+"F4.wireOp",EDGE,"E8.23.1"),sQuery(id+"F4.wireOp",EDGE,"E8.23.2"),sQuery(id+"F4.wireOp",EDGE,"E8.23.3"),sQuery(id+"F4.wireOp",EDGE,"E8.23.4"),sQuery(id+"F4.wireOp",EDGE,"E8.23.5")])]});
            var Q24;
            Q24=makeQuery(id+"F5.opExtrude","SWEPT_BODY",BODY,{"disambiguationData":[OSD([sQuery(id+"F4.wireOp",EDGE,"E8.24.0"),sQuery(id+"F4.wireOp",EDGE,"E8.24.1"),sQuery(id+"F4.wireOp",EDGE,"E8.24.2"),sQuery(id+"F4.wireOp",EDGE,"E8.24.3"),sQuery(id+"F4.wireOp",EDGE,"E8.24.4"),sQuery(id+"F4.wireOp",EDGE,"E8.24.5")])]});
            var Q25;
            Q25=makeQuery(id+"F5.opExtrude","SWEPT_BODY",BODY,{"disambiguationData":[OSD([sQuery(id+"F4.wireOp",EDGE,"E8.25.0"),sQuery(id+"F4.wireOp",EDGE,"E8.25.1"),sQuery(id+"F4.wireOp",EDGE,"E8.25.2"),sQuery(id+"F4.wireOp",EDGE,"E8.25.3"),sQuery(id+"F4.wireOp",EDGE,"E8.25.4"),sQuery(id+"F4.wireOp",EDGE,"E8.25.5")])]});
            var Q26;
            Q26=makeQuery(id+"F5.opExtrude","SWEPT_BODY",BODY,{"disambiguationData":[OSD([sQuery(id+"F4.wireOp",EDGE,"E8.26.0"),sQuery(id+"F4.wireOp",EDGE,"E8.26.1"),sQuery(id+"F4.wireOp",EDGE,"E8.26.2"),sQuery(id+"F4.wireOp",EDGE,"E8.26.3"),sQuery(id+"F4.wireOp",EDGE,"E8.26.4"),sQuery(id+"F4.wireOp",EDGE,"E8.26.5")])]});
            var Q27;
            Q27=makeQuery(id+"F5.opExtrude","SWEPT_BODY",BODY,{"disambiguationData":[OSD([sQuery(id+"F4.wireOp",EDGE,"E8.27.0"),sQuery(id+"F4.wireOp",EDGE,"E8.27.1"),sQuery(id+"F4.wireOp",EDGE,"E8.27.2"),sQuery(id+"F4.wireOp",EDGE,"E8.27.3"),sQuery(id+"F4.wireOp",EDGE,"E8.27.4"),sQuery(id+"F4.wireOp",EDGE,"E8.27.5")])]});
            var Q28;
            Q28=makeQuery(id+"F5.opExtrude","SWEPT_BODY",BODY,{"disambiguationData":[OSD([sQuery(id+"F4.wireOp",EDGE,"E8.28.0"),sQuery(id+"F4.wireOp",EDGE,"E8.28.1"),sQuery(id+"F4.wireOp",EDGE,"E8.28.2"),sQuery(id+"F4.wireOp",EDGE,"E8.28.3"),sQuery(id+"F4.wireOp",EDGE,"E8.28.4"),sQuery(id+"F4.wireOp",EDGE,"E8.28.5")])]});
            var Q29;
            Q29=makeQuery(id+"F5.opExtrude","SWEPT_BODY",BODY,{"disambiguationData":[OSD([sQuery(id+"F4.wireOp",EDGE,"E8.29.0"),sQuery(id+"F4.wireOp",EDGE,"E8.29.1"),sQuery(id+"F4.wireOp",EDGE,"E8.29.2"),sQuery(id+"F4.wireOp",EDGE,"E8.29.3"),sQuery(id+"F4.wireOp",EDGE,"E8.29.4"),sQuery(id+"F4.wireOp",EDGE,"E8.29.5")])]});
            var Q30;
            Q30=makeQuery(id+"F5.opExtrude","SWEPT_BODY",BODY,{"disambiguationData":[OSD([sQuery(id+"F4.wireOp",EDGE,"E8.30.0"),sQuery(id+"F4.wireOp",EDGE,"E8.30.1"),sQuery(id+"F4.wireOp",EDGE,"E8.30.2"),sQuery(id+"F4.wireOp",EDGE,"E8.30.3"),sQuery(id+"F4.wireOp",EDGE,"E8.30.4"),sQuery(id+"F4.wireOp",EDGE,"E8.30.5")])]});
            var Q31;
            Q31=makeQuery(id+"F5.opExtrude","SWEPT_BODY",BODY,{"disambiguationData":[OSD([sQuery(id+"F4.wireOp",EDGE,"E8.31.0"),sQuery(id+"F4.wireOp",EDGE,"E8.31.1"),sQuery(id+"F4.wireOp",EDGE,"E8.31.2"),sQuery(id+"F4.wireOp",EDGE,"E8.31.3"),sQuery(id+"F4.wireOp",EDGE,"E8.31.4"),sQuery(id+"F4.wireOp",EDGE,"E8.31.5")])]});
            var Q32;
            Q32=makeQuery(id+"F5.opExtrude","SWEPT_BODY",BODY,{"disambiguationData":[OSD([sQuery(id+"F4.wireOp",EDGE,"E8.32.0"),sQuery(id+"F4.wireOp",EDGE,"E8.32.1"),sQuery(id+"F4.wireOp",EDGE,"E8.32.2"),sQuery(id+"F4.wireOp",EDGE,"E8.32.3"),sQuery(id+"F4.wireOp",EDGE,"E8.32.4"),sQuery(id+"F4.wireOp",EDGE,"E8.32.5")])]});
            var Q33;
            Q33=makeQuery(id+"F5.opExtrude","SWEPT_BODY",BODY,{"disambiguationData":[OSD([sQuery(id+"F4.wireOp",EDGE,"E8.33.0"),sQuery(id+"F4.wireOp",EDGE,"E8.33.1"),sQuery(id+"F4.wireOp",EDGE,"E8.33.2"),sQuery(id+"F4.wireOp",EDGE,"E8.33.3"),sQuery(id+"F4.wireOp",EDGE,"E8.33.4"),sQuery(id+"F4.wireOp",EDGE,"E8.33.5")])]});
            var Q34;
            Q34=makeQuery(id+"F5.opExtrude","SWEPT_BODY",BODY,{"disambiguationData":[OSD([sQuery(id+"F4.wireOp",EDGE,"E8.34.0"),sQuery(id+"F4.wireOp",EDGE,"E8.34.1"),sQuery(id+"F4.wireOp",EDGE,"E8.34.2"),sQuery(id+"F4.wireOp",EDGE,"E8.34.3"),sQuery(id+"F4.wireOp",EDGE,"E8.34.4"),sQuery(id+"F4.wireOp",EDGE,"E8.34.5")])]});
            var Q35;
            Q35=makeQuery(id+"F5.opExtrude","SWEPT_BODY",BODY,{"disambiguationData":[OSD([sQuery(id+"F4.wireOp",EDGE,"E8.35.0"),sQuery(id+"F4.wireOp",EDGE,"E8.35.1"),sQuery(id+"F4.wireOp",EDGE,"E8.35.2"),sQuery(id+"F4.wireOp",EDGE,"E8.35.3"),sQuery(id+"F4.wireOp",EDGE,"E8.35.4"),sQuery(id+"F4.wireOp",EDGE,"E8.35.5")])]});
            var Q36;
            Q36=makeQuery(id+"F5.opExtrude","SWEPT_BODY",BODY,{"disambiguationData":[OSD([sQuery(id+"F4.wireOp",EDGE,"E8.36.0"),sQuery(id+"F4.wireOp",EDGE,"E8.36.1"),sQuery(id+"F4.wireOp",EDGE,"E8.36.2"),sQuery(id+"F4.wireOp",EDGE,"E8.36.3"),sQuery(id+"F4.wireOp",EDGE,"E8.36.4"),sQuery(id+"F4.wireOp",EDGE,"E8.36.5")])]});
            var Q37;
            Q37=makeQuery(id+"F5.opExtrude","SWEPT_BODY",BODY,{"disambiguationData":[OSD([sQuery(id+"F4.wireOp",EDGE,"E8.37.0"),sQuery(id+"F4.wireOp",EDGE,"E8.37.1"),sQuery(id+"F4.wireOp",EDGE,"E8.37.2"),sQuery(id+"F4.wireOp",EDGE,"E8.37.3"),sQuery(id+"F4.wireOp",EDGE,"E8.37.4"),sQuery(id+"F4.wireOp",EDGE,"E8.37.5")])]});
            var Q38;
            Q38=makeQuery(id+"F5.opExtrude","SWEPT_BODY",BODY,{"disambiguationData":[OSD([sQuery(id+"F4.wireOp",EDGE,"E8.38.0"),sQuery(id+"F4.wireOp",EDGE,"E8.38.1"),sQuery(id+"F4.wireOp",EDGE,"E8.38.2"),sQuery(id+"F4.wireOp",EDGE,"E8.38.3"),sQuery(id+"F4.wireOp",EDGE,"E8.38.4"),sQuery(id+"F4.wireOp",EDGE,"E8.38.5")])]});
            var Q39;
            Q39=makeQuery(id+"F5.opExtrude","SWEPT_BODY",BODY,{"disambiguationData":[OSD([sQuery(id+"F4.wireOp",EDGE,"E8.39.0"),sQuery(id+"F4.wireOp",EDGE,"E8.39.1"),sQuery(id+"F4.wireOp",EDGE,"E8.39.2"),sQuery(id+"F4.wireOp",EDGE,"E8.39.3"),sQuery(id+"F4.wireOp",EDGE,"E8.39.4"),sQuery(id+"F4.wireOp",EDGE,"E8.39.5")])]});
            var Q40;
            Q40=makeQuery(id+"F5.opExtrude","SWEPT_BODY",BODY,{"disambiguationData":[OSD([sQuery(id+"F4.wireOp",EDGE,"E8.40.0"),sQuery(id+"F4.wireOp",EDGE,"E8.40.1"),sQuery(id+"F4.wireOp",EDGE,"E8.40.2"),sQuery(id+"F4.wireOp",EDGE,"E8.40.3"),sQuery(id+"F4.wireOp",EDGE,"E8.40.4"),sQuery(id+"F4.wireOp",EDGE,"E8.40.5")])]});
            var Q41;
            Q41=makeQuery(id+"F5.opExtrude","SWEPT_BODY",BODY,{"disambiguationData":[OSD([sQuery(id+"F4.wireOp",EDGE,"E8.41.0"),sQuery(id+"F4.wireOp",EDGE,"E8.41.1"),sQuery(id+"F4.wireOp",EDGE,"E8.41.2"),sQuery(id+"F4.wireOp",EDGE,"E8.41.3"),sQuery(id+"F4.wireOp",EDGE,"E8.41.4"),sQuery(id+"F4.wireOp",EDGE,"E8.41.5")])]});
            var Q42;
            Q42=makeQuery(id+"F5.opExtrude","SWEPT_BODY",BODY,{"disambiguationData":[OSD([sQuery(id+"F4.wireOp",EDGE,"E8.42.0"),sQuery(id+"F4.wireOp",EDGE,"E8.42.1"),sQuery(id+"F4.wireOp",EDGE,"E8.42.2"),sQuery(id+"F4.wireOp",EDGE,"E8.42.3"),sQuery(id+"F4.wireOp",EDGE,"E8.42.4"),sQuery(id+"F4.wireOp",EDGE,"E8.42.5")])]});
            var Q43;
            Q43=makeQuery(id+"F5.opExtrude","SWEPT_BODY",BODY,{"disambiguationData":[OSD([sQuery(id+"F4.wireOp",EDGE,"E8.43.0"),sQuery(id+"F4.wireOp",EDGE,"E8.43.1"),sQuery(id+"F4.wireOp",EDGE,"E8.43.2"),sQuery(id+"F4.wireOp",EDGE,"E8.43.3"),sQuery(id+"F4.wireOp",EDGE,"E8.43.4"),sQuery(id+"F4.wireOp",EDGE,"E8.43.5")])]});
            var Q44;
            Q44=makeQuery(id+"F5.opExtrude","SWEPT_BODY",BODY,{"disambiguationData":[OSD([sQuery(id+"F4.wireOp",EDGE,"E8.44.0"),sQuery(id+"F4.wireOp",EDGE,"E8.44.1"),sQuery(id+"F4.wireOp",EDGE,"E8.44.2"),sQuery(id+"F4.wireOp",EDGE,"E8.44.3"),sQuery(id+"F4.wireOp",EDGE,"E8.44.4"),sQuery(id+"F4.wireOp",EDGE,"E8.44.5")])]});
            var Q45;
            Q45=makeQuery(id+"F5.opExtrude","SWEPT_BODY",BODY,{"disambiguationData":[OSD([sQuery(id+"F4.wireOp",EDGE,"E8.45.0"),sQuery(id+"F4.wireOp",EDGE,"E8.45.1"),sQuery(id+"F4.wireOp",EDGE,"E8.45.2"),sQuery(id+"F4.wireOp",EDGE,"E8.45.3"),sQuery(id+"F4.wireOp",EDGE,"E8.45.4"),sQuery(id+"F4.wireOp",EDGE,"E8.45.5")])]});
            var Q46;
            Q46=makeQuery(id+"F5.opExtrude","SWEPT_BODY",BODY,{"disambiguationData":[OSD([sQuery(id+"F4.wireOp",EDGE,"E8.46.0"),sQuery(id+"F4.wireOp",EDGE,"E8.46.1"),sQuery(id+"F4.wireOp",EDGE,"E8.46.2"),sQuery(id+"F4.wireOp",EDGE,"E8.46.3"),sQuery(id+"F4.wireOp",EDGE,"E8.46.4"),sQuery(id+"F4.wireOp",EDGE,"E8.46.5")])]});
            var Q47;
            Q47=makeQuery(id+"F5.opExtrude","SWEPT_BODY",BODY,{"disambiguationData":[OSD([sQuery(id+"F4.wireOp",EDGE,"E8.47.0"),sQuery(id+"F4.wireOp",EDGE,"E8.47.1"),sQuery(id+"F4.wireOp",EDGE,"E8.47.2"),sQuery(id+"F4.wireOp",EDGE,"E8.47.3"),sQuery(id+"F4.wireOp",EDGE,"E8.47.4"),sQuery(id+"F4.wireOp",EDGE,"E8.47.5")])]});
            var Q48;
            Q48=makeQuery(id+"F5.opExtrude","SWEPT_BODY",BODY,{"disambiguationData":[OSD([sQuery(id+"F4.wireOp",EDGE,"E8.48.0"),sQuery(id+"F4.wireOp",EDGE,"E8.48.1"),sQuery(id+"F4.wireOp",EDGE,"E8.48.2"),sQuery(id+"F4.wireOp",EDGE,"E8.48.3"),sQuery(id+"F4.wireOp",EDGE,"E8.48.4"),sQuery(id+"F4.wireOp",EDGE,"E8.48.5")])]});
            var Q49;
            Q49=makeQuery(id+"F5.opExtrude","SWEPT_BODY",BODY,{"disambiguationData":[OSD([sQuery(id+"F4.wireOp",EDGE,"E8.49.0"),sQuery(id+"F4.wireOp",EDGE,"E8.49.1"),sQuery(id+"F4.wireOp",EDGE,"E8.49.2"),sQuery(id+"F4.wireOp",EDGE,"E8.49.3"),sQuery(id+"F4.wireOp",EDGE,"E8.49.4"),sQuery(id+"F4.wireOp",EDGE,"E8.49.5")])]});
            var Q50;
            Q50=makeQuery(id+"F5.opExtrude","SWEPT_BODY",BODY,{"disambiguationData":[OSD([sQuery(id+"F4.wireOp",EDGE,"E8.50.0"),sQuery(id+"F4.wireOp",EDGE,"E8.50.1"),sQuery(id+"F4.wireOp",EDGE,"E8.50.2"),sQuery(id+"F4.wireOp",EDGE,"E8.50.3"),sQuery(id+"F4.wireOp",EDGE,"E8.50.4"),sQuery(id+"F4.wireOp",EDGE,"E8.50.5")])]});
            var Q51;
            Q51=makeQuery(id+"F5.opExtrude","SWEPT_BODY",BODY,{"disambiguationData":[OSD([sQuery(id+"F4.wireOp",EDGE,"E8.51.0"),sQuery(id+"F4.wireOp",EDGE,"E8.51.1"),sQuery(id+"F4.wireOp",EDGE,"E8.51.2"),sQuery(id+"F4.wireOp",EDGE,"E8.51.3"),sQuery(id+"F4.wireOp",EDGE,"E8.51.4"),sQuery(id+"F4.wireOp",EDGE,"E8.51.5")])]});
            var Q52;
            Q52=makeQuery(id+"F5.opExtrude","SWEPT_BODY",BODY,{"disambiguationData":[OSD([sQuery(id+"F4.wireOp",EDGE,"E8.52.0"),sQuery(id+"F4.wireOp",EDGE,"E8.52.1"),sQuery(id+"F4.wireOp",EDGE,"E8.52.2"),sQuery(id+"F4.wireOp",EDGE,"E8.52.3"),sQuery(id+"F4.wireOp",EDGE,"E8.52.4"),sQuery(id+"F4.wireOp",EDGE,"E8.52.5")])]});
            var Q53;
            Q53=makeQuery(id+"F5.opExtrude","SWEPT_BODY",BODY,{"disambiguationData":[OSD([sQuery(id+"F4.wireOp",EDGE,"E8.53.0"),sQuery(id+"F4.wireOp",EDGE,"E8.53.1"),sQuery(id+"F4.wireOp",EDGE,"E8.53.2"),sQuery(id+"F4.wireOp",EDGE,"E8.53.3"),sQuery(id+"F4.wireOp",EDGE,"E8.53.4"),sQuery(id+"F4.wireOp",EDGE,"E8.53.5")])]});
            var Q54;
            Q54=makeQuery(id+"F5.opExtrude","SWEPT_BODY",BODY,{"disambiguationData":[OSD([sQuery(id+"F4.wireOp",EDGE,"E8.54.0"),sQuery(id+"F4.wireOp",EDGE,"E8.54.1"),sQuery(id+"F4.wireOp",EDGE,"E8.54.2"),sQuery(id+"F4.wireOp",EDGE,"E8.54.3"),sQuery(id+"F4.wireOp",EDGE,"E8.54.4"),sQuery(id+"F4.wireOp",EDGE,"E8.54.5")])]});
            var Q55;
            Q55=makeQuery(id+"F5.opExtrude","SWEPT_BODY",BODY,{"disambiguationData":[OSD([sQuery(id+"F4.wireOp",EDGE,"E8.55.0"),sQuery(id+"F4.wireOp",EDGE,"E8.55.1"),sQuery(id+"F4.wireOp",EDGE,"E8.55.2"),sQuery(id+"F4.wireOp",EDGE,"E8.55.3"),sQuery(id+"F4.wireOp",EDGE,"E8.55.4"),sQuery(id+"F4.wireOp",EDGE,"E8.55.5")])]});
            var Q56;
            Q56=makeQuery(id+"F5.opExtrude","SWEPT_BODY",BODY,{"disambiguationData":[OSD([sQuery(id+"F4.wireOp",EDGE,"E8.56.0"),sQuery(id+"F4.wireOp",EDGE,"E8.56.1"),sQuery(id+"F4.wireOp",EDGE,"E8.56.2"),sQuery(id+"F4.wireOp",EDGE,"E8.56.3"),sQuery(id+"F4.wireOp",EDGE,"E8.56.4"),sQuery(id+"F4.wireOp",EDGE,"E8.56.5")])]});
            var Q57;
            Q57=makeQuery(id+"F5.opExtrude","SWEPT_BODY",BODY,{"disambiguationData":[OSD([sQuery(id+"F4.wireOp",EDGE,"E8.57.0"),sQuery(id+"F4.wireOp",EDGE,"E8.57.1"),sQuery(id+"F4.wireOp",EDGE,"E8.57.2"),sQuery(id+"F4.wireOp",EDGE,"E8.57.3"),sQuery(id+"F4.wireOp",EDGE,"E8.57.4"),sQuery(id+"F4.wireOp",EDGE,"E8.57.5")])]});
            var Q58;
            Q58=makeQuery(id+"F5.opExtrude","SWEPT_BODY",BODY,{"disambiguationData":[OSD([sQuery(id+"F4.wireOp",EDGE,"E8.58.0"),sQuery(id+"F4.wireOp",EDGE,"E8.58.1"),sQuery(id+"F4.wireOp",EDGE,"E8.58.2"),sQuery(id+"F4.wireOp",EDGE,"E8.58.3"),sQuery(id+"F4.wireOp",EDGE,"E8.58.4"),sQuery(id+"F4.wireOp",EDGE,"E8.58.5")])]});
            var Q59;
            Q59=makeQuery(id+"F5.opExtrude","SWEPT_BODY",BODY,{"disambiguationData":[OSD([sQuery(id+"F4.wireOp",EDGE,"E8.59.0"),sQuery(id+"F4.wireOp",EDGE,"E8.59.1"),sQuery(id+"F4.wireOp",EDGE,"E8.59.2"),sQuery(id+"F4.wireOp",EDGE,"E8.59.3"),sQuery(id+"F4.wireOp",EDGE,"E8.59.4"),sQuery(id+"F4.wireOp",EDGE,"E8.59.5")])]});
            transform(context, id + "F6", {"entities" : qUnion([Q0, Q1, Q2, Q3, Q4, Q5, Q6, Q7, Q8, Q9, Q10, Q11, Q12, Q13, Q14, Q15, Q16, Q17, Q18, Q19, Q20, Q21, Q22, Q23, Q24, Q25, Q26, Q27, Q28, Q29, Q30, Q31, Q32, Q33, Q34, Q35, Q36, Q37, Q38, Q39, Q40, Q41, Q42, Q43, Q44, Q45, Q46, Q47, Q48, Q49, Q50, Q51, Q52, Q53, Q54, Q55, Q56, Q57, Q58, Q59]), "transformType" : TransformType.TRANSLATION_3D, "dx" : 0 * mm, "dy" : 0 * mm, "dz" : 1.91 * mm, "makeCopy" : false});
        }
        {
            var Q0;
            Q0=makeQuery(id+"F5.opExtrude","SWEPT_BODY",BODY,{"disambiguationData":[OSD([sQuery(id+"F4.wireOp",EDGE,"E2"),sQuery(id+"F4.wireOp",EDGE,"E3"),sQuery(id+"F4.wireOp",EDGE,"E4"),sQuery(id+"F4.wireOp",EDGE,"E5"),sQuery(id+"F4.wireOp",EDGE,"E6"),sQuery(id+"F4.wireOp",EDGE,"E7")])]});
            var Q1;
            Q1=makeQuery(id+"F5.opExtrude","SWEPT_BODY",BODY,{"disambiguationData":[OSD([sQuery(id+"F4.wireOp",EDGE,"E8.1.0"),sQuery(id+"F4.wireOp",EDGE,"E8.1.1"),sQuery(id+"F4.wireOp",EDGE,"E8.1.2"),sQuery(id+"F4.wireOp",EDGE,"E8.1.3"),sQuery(id+"F4.wireOp",EDGE,"E8.1.4"),sQuery(id+"F4.wireOp",EDGE,"E8.1.5")])]});
            var Q2;
            Q2=makeQuery(id+"F5.opExtrude","SWEPT_BODY",BODY,{"disambiguationData":[OSD([sQuery(id+"F4.wireOp",EDGE,"E8.2.0"),sQuery(id+"F4.wireOp",EDGE,"E8.2.1"),sQuery(id+"F4.wireOp",EDGE,"E8.2.2"),sQuery(id+"F4.wireOp",EDGE,"E8.2.3"),sQuery(id+"F4.wireOp",EDGE,"E8.2.4"),sQuery(id+"F4.wireOp",EDGE,"E8.2.5")])]});
            var Q3;
            Q3=makeQuery(id+"F5.opExtrude","SWEPT_BODY",BODY,{"disambiguationData":[OSD([sQuery(id+"F4.wireOp",EDGE,"E8.3.0"),sQuery(id+"F4.wireOp",EDGE,"E8.3.1"),sQuery(id+"F4.wireOp",EDGE,"E8.3.2"),sQuery(id+"F4.wireOp",EDGE,"E8.3.3"),sQuery(id+"F4.wireOp",EDGE,"E8.3.4"),sQuery(id+"F4.wireOp",EDGE,"E8.3.5")])]});
            var Q4;
            Q4=makeQuery(id+"F5.opExtrude","SWEPT_BODY",BODY,{"disambiguationData":[OSD([sQuery(id+"F4.wireOp",EDGE,"E8.4.0"),sQuery(id+"F4.wireOp",EDGE,"E8.4.1"),sQuery(id+"F4.wireOp",EDGE,"E8.4.2"),sQuery(id+"F4.wireOp",EDGE,"E8.4.3"),sQuery(id+"F4.wireOp",EDGE,"E8.4.4"),sQuery(id+"F4.wireOp",EDGE,"E8.4.5")])]});
            var Q5;
            Q5=makeQuery(id+"F5.opExtrude","SWEPT_BODY",BODY,{"disambiguationData":[OSD([sQuery(id+"F4.wireOp",EDGE,"E8.5.0"),sQuery(id+"F4.wireOp",EDGE,"E8.5.1"),sQuery(id+"F4.wireOp",EDGE,"E8.5.2"),sQuery(id+"F4.wireOp",EDGE,"E8.5.3"),sQuery(id+"F4.wireOp",EDGE,"E8.5.4"),sQuery(id+"F4.wireOp",EDGE,"E8.5.5")])]});
            var Q6;
            Q6=makeQuery(id+"F5.opExtrude","SWEPT_BODY",BODY,{"disambiguationData":[OSD([sQuery(id+"F4.wireOp",EDGE,"E8.6.0"),sQuery(id+"F4.wireOp",EDGE,"E8.6.1"),sQuery(id+"F4.wireOp",EDGE,"E8.6.2"),sQuery(id+"F4.wireOp",EDGE,"E8.6.3"),sQuery(id+"F4.wireOp",EDGE,"E8.6.4"),sQuery(id+"F4.wireOp",EDGE,"E8.6.5")])]});
            var Q7;
            Q7=makeQuery(id+"F5.opExtrude","SWEPT_BODY",BODY,{"disambiguationData":[OSD([sQuery(id+"F4.wireOp",EDGE,"E8.7.0"),sQuery(id+"F4.wireOp",EDGE,"E8.7.1"),sQuery(id+"F4.wireOp",EDGE,"E8.7.2"),sQuery(id+"F4.wireOp",EDGE,"E8.7.3"),sQuery(id+"F4.wireOp",EDGE,"E8.7.4"),sQuery(id+"F4.wireOp",EDGE,"E8.7.5")])]});
            var Q8;
            Q8=makeQuery(id+"F5.opExtrude","SWEPT_BODY",BODY,{"disambiguationData":[OSD([sQuery(id+"F4.wireOp",EDGE,"E8.8.0"),sQuery(id+"F4.wireOp",EDGE,"E8.8.1"),sQuery(id+"F4.wireOp",EDGE,"E8.8.2"),sQuery(id+"F4.wireOp",EDGE,"E8.8.3"),sQuery(id+"F4.wireOp",EDGE,"E8.8.4"),sQuery(id+"F4.wireOp",EDGE,"E8.8.5")])]});
            var Q9;
            Q9=makeQuery(id+"F5.opExtrude","SWEPT_BODY",BODY,{"disambiguationData":[OSD([sQuery(id+"F4.wireOp",EDGE,"E8.9.0"),sQuery(id+"F4.wireOp",EDGE,"E8.9.1"),sQuery(id+"F4.wireOp",EDGE,"E8.9.2"),sQuery(id+"F4.wireOp",EDGE,"E8.9.3"),sQuery(id+"F4.wireOp",EDGE,"E8.9.4"),sQuery(id+"F4.wireOp",EDGE,"E8.9.5")])]});
            var Q10;
            Q10=makeQuery(id+"F5.opExtrude","SWEPT_BODY",BODY,{"disambiguationData":[OSD([sQuery(id+"F4.wireOp",EDGE,"E8.10.0"),sQuery(id+"F4.wireOp",EDGE,"E8.10.1"),sQuery(id+"F4.wireOp",EDGE,"E8.10.2"),sQuery(id+"F4.wireOp",EDGE,"E8.10.3"),sQuery(id+"F4.wireOp",EDGE,"E8.10.4"),sQuery(id+"F4.wireOp",EDGE,"E8.10.5")])]});
            var Q11;
            Q11=makeQuery(id+"F5.opExtrude","SWEPT_BODY",BODY,{"disambiguationData":[OSD([sQuery(id+"F4.wireOp",EDGE,"E8.11.0"),sQuery(id+"F4.wireOp",EDGE,"E8.11.1"),sQuery(id+"F4.wireOp",EDGE,"E8.11.2"),sQuery(id+"F4.wireOp",EDGE,"E8.11.3"),sQuery(id+"F4.wireOp",EDGE,"E8.11.4"),sQuery(id+"F4.wireOp",EDGE,"E8.11.5")])]});
            var Q12;
            Q12=makeQuery(id+"F5.opExtrude","SWEPT_BODY",BODY,{"disambiguationData":[OSD([sQuery(id+"F4.wireOp",EDGE,"E8.12.0"),sQuery(id+"F4.wireOp",EDGE,"E8.12.1"),sQuery(id+"F4.wireOp",EDGE,"E8.12.2"),sQuery(id+"F4.wireOp",EDGE,"E8.12.3"),sQuery(id+"F4.wireOp",EDGE,"E8.12.4"),sQuery(id+"F4.wireOp",EDGE,"E8.12.5")])]});
            var Q13;
            Q13=makeQuery(id+"F5.opExtrude","SWEPT_BODY",BODY,{"disambiguationData":[OSD([sQuery(id+"F4.wireOp",EDGE,"E8.13.0"),sQuery(id+"F4.wireOp",EDGE,"E8.13.1"),sQuery(id+"F4.wireOp",EDGE,"E8.13.2"),sQuery(id+"F4.wireOp",EDGE,"E8.13.3"),sQuery(id+"F4.wireOp",EDGE,"E8.13.4"),sQuery(id+"F4.wireOp",EDGE,"E8.13.5")])]});
            var Q14;
            Q14=makeQuery(id+"F5.opExtrude","SWEPT_BODY",BODY,{"disambiguationData":[OSD([sQuery(id+"F4.wireOp",EDGE,"E8.14.0"),sQuery(id+"F4.wireOp",EDGE,"E8.14.1"),sQuery(id+"F4.wireOp",EDGE,"E8.14.2"),sQuery(id+"F4.wireOp",EDGE,"E8.14.3"),sQuery(id+"F4.wireOp",EDGE,"E8.14.4"),sQuery(id+"F4.wireOp",EDGE,"E8.14.5")])]});
            var Q15;
            Q15=makeQuery(id+"F5.opExtrude","SWEPT_BODY",BODY,{"disambiguationData":[OSD([sQuery(id+"F4.wireOp",EDGE,"E8.15.0"),sQuery(id+"F4.wireOp",EDGE,"E8.15.1"),sQuery(id+"F4.wireOp",EDGE,"E8.15.2"),sQuery(id+"F4.wireOp",EDGE,"E8.15.3"),sQuery(id+"F4.wireOp",EDGE,"E8.15.4"),sQuery(id+"F4.wireOp",EDGE,"E8.15.5")])]});
            var Q16;
            Q16=makeQuery(id+"F5.opExtrude","SWEPT_BODY",BODY,{"disambiguationData":[OSD([sQuery(id+"F4.wireOp",EDGE,"E8.16.0"),sQuery(id+"F4.wireOp",EDGE,"E8.16.1"),sQuery(id+"F4.wireOp",EDGE,"E8.16.2"),sQuery(id+"F4.wireOp",EDGE,"E8.16.3"),sQuery(id+"F4.wireOp",EDGE,"E8.16.4"),sQuery(id+"F4.wireOp",EDGE,"E8.16.5")])]});
            var Q17;
            Q17=makeQuery(id+"F5.opExtrude","SWEPT_BODY",BODY,{"disambiguationData":[OSD([sQuery(id+"F4.wireOp",EDGE,"E8.17.0"),sQuery(id+"F4.wireOp",EDGE,"E8.17.1"),sQuery(id+"F4.wireOp",EDGE,"E8.17.2"),sQuery(id+"F4.wireOp",EDGE,"E8.17.3"),sQuery(id+"F4.wireOp",EDGE,"E8.17.4"),sQuery(id+"F4.wireOp",EDGE,"E8.17.5")])]});
            var Q18;
            Q18=makeQuery(id+"F5.opExtrude","SWEPT_BODY",BODY,{"disambiguationData":[OSD([sQuery(id+"F4.wireOp",EDGE,"E8.18.0"),sQuery(id+"F4.wireOp",EDGE,"E8.18.1"),sQuery(id+"F4.wireOp",EDGE,"E8.18.2"),sQuery(id+"F4.wireOp",EDGE,"E8.18.3"),sQuery(id+"F4.wireOp",EDGE,"E8.18.4"),sQuery(id+"F4.wireOp",EDGE,"E8.18.5")])]});
            var Q19;
            Q19=makeQuery(id+"F5.opExtrude","SWEPT_BODY",BODY,{"disambiguationData":[OSD([sQuery(id+"F4.wireOp",EDGE,"E8.19.0"),sQuery(id+"F4.wireOp",EDGE,"E8.19.1"),sQuery(id+"F4.wireOp",EDGE,"E8.19.2"),sQuery(id+"F4.wireOp",EDGE,"E8.19.3"),sQuery(id+"F4.wireOp",EDGE,"E8.19.4"),sQuery(id+"F4.wireOp",EDGE,"E8.19.5")])]});
            var Q20;
            Q20=makeQuery(id+"F5.opExtrude","SWEPT_BODY",BODY,{"disambiguationData":[OSD([sQuery(id+"F4.wireOp",EDGE,"E8.20.0"),sQuery(id+"F4.wireOp",EDGE,"E8.20.1"),sQuery(id+"F4.wireOp",EDGE,"E8.20.2"),sQuery(id+"F4.wireOp",EDGE,"E8.20.3"),sQuery(id+"F4.wireOp",EDGE,"E8.20.4"),sQuery(id+"F4.wireOp",EDGE,"E8.20.5")])]});
            var Q21;
            Q21=makeQuery(id+"F5.opExtrude","SWEPT_BODY",BODY,{"disambiguationData":[OSD([sQuery(id+"F4.wireOp",EDGE,"E8.21.0"),sQuery(id+"F4.wireOp",EDGE,"E8.21.1"),sQuery(id+"F4.wireOp",EDGE,"E8.21.2"),sQuery(id+"F4.wireOp",EDGE,"E8.21.3"),sQuery(id+"F4.wireOp",EDGE,"E8.21.4"),sQuery(id+"F4.wireOp",EDGE,"E8.21.5")])]});
            var Q22;
            Q22=makeQuery(id+"F5.opExtrude","SWEPT_BODY",BODY,{"disambiguationData":[OSD([sQuery(id+"F4.wireOp",EDGE,"E8.22.0"),sQuery(id+"F4.wireOp",EDGE,"E8.22.1"),sQuery(id+"F4.wireOp",EDGE,"E8.22.2"),sQuery(id+"F4.wireOp",EDGE,"E8.22.3"),sQuery(id+"F4.wireOp",EDGE,"E8.22.4"),sQuery(id+"F4.wireOp",EDGE,"E8.22.5")])]});
            var Q23;
            Q23=makeQuery(id+"F5.opExtrude","SWEPT_BODY",BODY,{"disambiguationData":[OSD([sQuery(id+"F4.wireOp",EDGE,"E8.23.0"),sQuery(id+"F4.wireOp",EDGE,"E8.23.1"),sQuery(id+"F4.wireOp",EDGE,"E8.23.2"),sQuery(id+"F4.wireOp",EDGE,"E8.23.3"),sQuery(id+"F4.wireOp",EDGE,"E8.23.4"),sQuery(id+"F4.wireOp",EDGE,"E8.23.5")])]});
            var Q24;
            Q24=makeQuery(id+"F5.opExtrude","SWEPT_BODY",BODY,{"disambiguationData":[OSD([sQuery(id+"F4.wireOp",EDGE,"E8.24.0"),sQuery(id+"F4.wireOp",EDGE,"E8.24.1"),sQuery(id+"F4.wireOp",EDGE,"E8.24.2"),sQuery(id+"F4.wireOp",EDGE,"E8.24.3"),sQuery(id+"F4.wireOp",EDGE,"E8.24.4"),sQuery(id+"F4.wireOp",EDGE,"E8.24.5")])]});
            var Q25;
            Q25=makeQuery(id+"F5.opExtrude","SWEPT_BODY",BODY,{"disambiguationData":[OSD([sQuery(id+"F4.wireOp",EDGE,"E8.25.0"),sQuery(id+"F4.wireOp",EDGE,"E8.25.1"),sQuery(id+"F4.wireOp",EDGE,"E8.25.2"),sQuery(id+"F4.wireOp",EDGE,"E8.25.3"),sQuery(id+"F4.wireOp",EDGE,"E8.25.4"),sQuery(id+"F4.wireOp",EDGE,"E8.25.5")])]});
            var Q26;
            Q26=makeQuery(id+"F5.opExtrude","SWEPT_BODY",BODY,{"disambiguationData":[OSD([sQuery(id+"F4.wireOp",EDGE,"E8.26.0"),sQuery(id+"F4.wireOp",EDGE,"E8.26.1"),sQuery(id+"F4.wireOp",EDGE,"E8.26.2"),sQuery(id+"F4.wireOp",EDGE,"E8.26.3"),sQuery(id+"F4.wireOp",EDGE,"E8.26.4"),sQuery(id+"F4.wireOp",EDGE,"E8.26.5")])]});
            var Q27;
            Q27=makeQuery(id+"F5.opExtrude","SWEPT_BODY",BODY,{"disambiguationData":[OSD([sQuery(id+"F4.wireOp",EDGE,"E8.27.0"),sQuery(id+"F4.wireOp",EDGE,"E8.27.1"),sQuery(id+"F4.wireOp",EDGE,"E8.27.2"),sQuery(id+"F4.wireOp",EDGE,"E8.27.3"),sQuery(id+"F4.wireOp",EDGE,"E8.27.4"),sQuery(id+"F4.wireOp",EDGE,"E8.27.5")])]});
            var Q28;
            Q28=makeQuery(id+"F5.opExtrude","SWEPT_BODY",BODY,{"disambiguationData":[OSD([sQuery(id+"F4.wireOp",EDGE,"E8.28.0"),sQuery(id+"F4.wireOp",EDGE,"E8.28.1"),sQuery(id+"F4.wireOp",EDGE,"E8.28.2"),sQuery(id+"F4.wireOp",EDGE,"E8.28.3"),sQuery(id+"F4.wireOp",EDGE,"E8.28.4"),sQuery(id+"F4.wireOp",EDGE,"E8.28.5")])]});
            var Q29;
            Q29=makeQuery(id+"F5.opExtrude","SWEPT_BODY",BODY,{"disambiguationData":[OSD([sQuery(id+"F4.wireOp",EDGE,"E8.29.0"),sQuery(id+"F4.wireOp",EDGE,"E8.29.1"),sQuery(id+"F4.wireOp",EDGE,"E8.29.2"),sQuery(id+"F4.wireOp",EDGE,"E8.29.3"),sQuery(id+"F4.wireOp",EDGE,"E8.29.4"),sQuery(id+"F4.wireOp",EDGE,"E8.29.5")])]});
            var Q30;
            Q30=makeQuery(id+"F5.opExtrude","SWEPT_BODY",BODY,{"disambiguationData":[OSD([sQuery(id+"F4.wireOp",EDGE,"E8.30.0"),sQuery(id+"F4.wireOp",EDGE,"E8.30.1"),sQuery(id+"F4.wireOp",EDGE,"E8.30.2"),sQuery(id+"F4.wireOp",EDGE,"E8.30.3"),sQuery(id+"F4.wireOp",EDGE,"E8.30.4"),sQuery(id+"F4.wireOp",EDGE,"E8.30.5")])]});
            var Q31;
            Q31=makeQuery(id+"F5.opExtrude","SWEPT_BODY",BODY,{"disambiguationData":[OSD([sQuery(id+"F4.wireOp",EDGE,"E8.31.0"),sQuery(id+"F4.wireOp",EDGE,"E8.31.1"),sQuery(id+"F4.wireOp",EDGE,"E8.31.2"),sQuery(id+"F4.wireOp",EDGE,"E8.31.3"),sQuery(id+"F4.wireOp",EDGE,"E8.31.4"),sQuery(id+"F4.wireOp",EDGE,"E8.31.5")])]});
            var Q32;
            Q32=makeQuery(id+"F5.opExtrude","SWEPT_BODY",BODY,{"disambiguationData":[OSD([sQuery(id+"F4.wireOp",EDGE,"E8.32.0"),sQuery(id+"F4.wireOp",EDGE,"E8.32.1"),sQuery(id+"F4.wireOp",EDGE,"E8.32.2"),sQuery(id+"F4.wireOp",EDGE,"E8.32.3"),sQuery(id+"F4.wireOp",EDGE,"E8.32.4"),sQuery(id+"F4.wireOp",EDGE,"E8.32.5")])]});
            var Q33;
            Q33=makeQuery(id+"F5.opExtrude","SWEPT_BODY",BODY,{"disambiguationData":[OSD([sQuery(id+"F4.wireOp",EDGE,"E8.33.0"),sQuery(id+"F4.wireOp",EDGE,"E8.33.1"),sQuery(id+"F4.wireOp",EDGE,"E8.33.2"),sQuery(id+"F4.wireOp",EDGE,"E8.33.3"),sQuery(id+"F4.wireOp",EDGE,"E8.33.4"),sQuery(id+"F4.wireOp",EDGE,"E8.33.5")])]});
            var Q34;
            Q34=makeQuery(id+"F5.opExtrude","SWEPT_BODY",BODY,{"disambiguationData":[OSD([sQuery(id+"F4.wireOp",EDGE,"E8.34.0"),sQuery(id+"F4.wireOp",EDGE,"E8.34.1"),sQuery(id+"F4.wireOp",EDGE,"E8.34.2"),sQuery(id+"F4.wireOp",EDGE,"E8.34.3"),sQuery(id+"F4.wireOp",EDGE,"E8.34.4"),sQuery(id+"F4.wireOp",EDGE,"E8.34.5")])]});
            var Q35;
            Q35=makeQuery(id+"F5.opExtrude","SWEPT_BODY",BODY,{"disambiguationData":[OSD([sQuery(id+"F4.wireOp",EDGE,"E8.35.0"),sQuery(id+"F4.wireOp",EDGE,"E8.35.1"),sQuery(id+"F4.wireOp",EDGE,"E8.35.2"),sQuery(id+"F4.wireOp",EDGE,"E8.35.3"),sQuery(id+"F4.wireOp",EDGE,"E8.35.4"),sQuery(id+"F4.wireOp",EDGE,"E8.35.5")])]});
            var Q36;
            Q36=makeQuery(id+"F5.opExtrude","SWEPT_BODY",BODY,{"disambiguationData":[OSD([sQuery(id+"F4.wireOp",EDGE,"E8.36.0"),sQuery(id+"F4.wireOp",EDGE,"E8.36.1"),sQuery(id+"F4.wireOp",EDGE,"E8.36.2"),sQuery(id+"F4.wireOp",EDGE,"E8.36.3"),sQuery(id+"F4.wireOp",EDGE,"E8.36.4"),sQuery(id+"F4.wireOp",EDGE,"E8.36.5")])]});
            var Q37;
            Q37=makeQuery(id+"F5.opExtrude","SWEPT_BODY",BODY,{"disambiguationData":[OSD([sQuery(id+"F4.wireOp",EDGE,"E8.37.0"),sQuery(id+"F4.wireOp",EDGE,"E8.37.1"),sQuery(id+"F4.wireOp",EDGE,"E8.37.2"),sQuery(id+"F4.wireOp",EDGE,"E8.37.3"),sQuery(id+"F4.wireOp",EDGE,"E8.37.4"),sQuery(id+"F4.wireOp",EDGE,"E8.37.5")])]});
            var Q38;
            Q38=makeQuery(id+"F5.opExtrude","SWEPT_BODY",BODY,{"disambiguationData":[OSD([sQuery(id+"F4.wireOp",EDGE,"E8.38.0"),sQuery(id+"F4.wireOp",EDGE,"E8.38.1"),sQuery(id+"F4.wireOp",EDGE,"E8.38.2"),sQuery(id+"F4.wireOp",EDGE,"E8.38.3"),sQuery(id+"F4.wireOp",EDGE,"E8.38.4"),sQuery(id+"F4.wireOp",EDGE,"E8.38.5")])]});
            var Q39;
            Q39=makeQuery(id+"F5.opExtrude","SWEPT_BODY",BODY,{"disambiguationData":[OSD([sQuery(id+"F4.wireOp",EDGE,"E8.39.0"),sQuery(id+"F4.wireOp",EDGE,"E8.39.1"),sQuery(id+"F4.wireOp",EDGE,"E8.39.2"),sQuery(id+"F4.wireOp",EDGE,"E8.39.3"),sQuery(id+"F4.wireOp",EDGE,"E8.39.4"),sQuery(id+"F4.wireOp",EDGE,"E8.39.5")])]});
            var Q40;
            Q40=makeQuery(id+"F5.opExtrude","SWEPT_BODY",BODY,{"disambiguationData":[OSD([sQuery(id+"F4.wireOp",EDGE,"E8.40.0"),sQuery(id+"F4.wireOp",EDGE,"E8.40.1"),sQuery(id+"F4.wireOp",EDGE,"E8.40.2"),sQuery(id+"F4.wireOp",EDGE,"E8.40.3"),sQuery(id+"F4.wireOp",EDGE,"E8.40.4"),sQuery(id+"F4.wireOp",EDGE,"E8.40.5")])]});
            var Q41;
            Q41=makeQuery(id+"F5.opExtrude","SWEPT_BODY",BODY,{"disambiguationData":[OSD([sQuery(id+"F4.wireOp",EDGE,"E8.41.0"),sQuery(id+"F4.wireOp",EDGE,"E8.41.1"),sQuery(id+"F4.wireOp",EDGE,"E8.41.2"),sQuery(id+"F4.wireOp",EDGE,"E8.41.3"),sQuery(id+"F4.wireOp",EDGE,"E8.41.4"),sQuery(id+"F4.wireOp",EDGE,"E8.41.5")])]});
            var Q42;
            Q42=makeQuery(id+"F5.opExtrude","SWEPT_BODY",BODY,{"disambiguationData":[OSD([sQuery(id+"F4.wireOp",EDGE,"E8.42.0"),sQuery(id+"F4.wireOp",EDGE,"E8.42.1"),sQuery(id+"F4.wireOp",EDGE,"E8.42.2"),sQuery(id+"F4.wireOp",EDGE,"E8.42.3"),sQuery(id+"F4.wireOp",EDGE,"E8.42.4"),sQuery(id+"F4.wireOp",EDGE,"E8.42.5")])]});
            var Q43;
            Q43=makeQuery(id+"F5.opExtrude","SWEPT_BODY",BODY,{"disambiguationData":[OSD([sQuery(id+"F4.wireOp",EDGE,"E8.43.0"),sQuery(id+"F4.wireOp",EDGE,"E8.43.1"),sQuery(id+"F4.wireOp",EDGE,"E8.43.2"),sQuery(id+"F4.wireOp",EDGE,"E8.43.3"),sQuery(id+"F4.wireOp",EDGE,"E8.43.4"),sQuery(id+"F4.wireOp",EDGE,"E8.43.5")])]});
            var Q44;
            Q44=makeQuery(id+"F5.opExtrude","SWEPT_BODY",BODY,{"disambiguationData":[OSD([sQuery(id+"F4.wireOp",EDGE,"E8.44.0"),sQuery(id+"F4.wireOp",EDGE,"E8.44.1"),sQuery(id+"F4.wireOp",EDGE,"E8.44.2"),sQuery(id+"F4.wireOp",EDGE,"E8.44.3"),sQuery(id+"F4.wireOp",EDGE,"E8.44.4"),sQuery(id+"F4.wireOp",EDGE,"E8.44.5")])]});
            var Q45;
            Q45=makeQuery(id+"F5.opExtrude","SWEPT_BODY",BODY,{"disambiguationData":[OSD([sQuery(id+"F4.wireOp",EDGE,"E8.45.0"),sQuery(id+"F4.wireOp",EDGE,"E8.45.1"),sQuery(id+"F4.wireOp",EDGE,"E8.45.2"),sQuery(id+"F4.wireOp",EDGE,"E8.45.3"),sQuery(id+"F4.wireOp",EDGE,"E8.45.4"),sQuery(id+"F4.wireOp",EDGE,"E8.45.5")])]});
            var Q46;
            Q46=makeQuery(id+"F5.opExtrude","SWEPT_BODY",BODY,{"disambiguationData":[OSD([sQuery(id+"F4.wireOp",EDGE,"E8.46.0"),sQuery(id+"F4.wireOp",EDGE,"E8.46.1"),sQuery(id+"F4.wireOp",EDGE,"E8.46.2"),sQuery(id+"F4.wireOp",EDGE,"E8.46.3"),sQuery(id+"F4.wireOp",EDGE,"E8.46.4"),sQuery(id+"F4.wireOp",EDGE,"E8.46.5")])]});
            var Q47;
            Q47=makeQuery(id+"F5.opExtrude","SWEPT_BODY",BODY,{"disambiguationData":[OSD([sQuery(id+"F4.wireOp",EDGE,"E8.47.0"),sQuery(id+"F4.wireOp",EDGE,"E8.47.1"),sQuery(id+"F4.wireOp",EDGE,"E8.47.2"),sQuery(id+"F4.wireOp",EDGE,"E8.47.3"),sQuery(id+"F4.wireOp",EDGE,"E8.47.4"),sQuery(id+"F4.wireOp",EDGE,"E8.47.5")])]});
            var Q48;
            Q48=makeQuery(id+"F5.opExtrude","SWEPT_BODY",BODY,{"disambiguationData":[OSD([sQuery(id+"F4.wireOp",EDGE,"E8.48.0"),sQuery(id+"F4.wireOp",EDGE,"E8.48.1"),sQuery(id+"F4.wireOp",EDGE,"E8.48.2"),sQuery(id+"F4.wireOp",EDGE,"E8.48.3"),sQuery(id+"F4.wireOp",EDGE,"E8.48.4"),sQuery(id+"F4.wireOp",EDGE,"E8.48.5")])]});
            var Q49;
            Q49=makeQuery(id+"F5.opExtrude","SWEPT_BODY",BODY,{"disambiguationData":[OSD([sQuery(id+"F4.wireOp",EDGE,"E8.49.0"),sQuery(id+"F4.wireOp",EDGE,"E8.49.1"),sQuery(id+"F4.wireOp",EDGE,"E8.49.2"),sQuery(id+"F4.wireOp",EDGE,"E8.49.3"),sQuery(id+"F4.wireOp",EDGE,"E8.49.4"),sQuery(id+"F4.wireOp",EDGE,"E8.49.5")])]});
            var Q50;
            Q50=makeQuery(id+"F5.opExtrude","SWEPT_BODY",BODY,{"disambiguationData":[OSD([sQuery(id+"F4.wireOp",EDGE,"E8.50.0"),sQuery(id+"F4.wireOp",EDGE,"E8.50.1"),sQuery(id+"F4.wireOp",EDGE,"E8.50.2"),sQuery(id+"F4.wireOp",EDGE,"E8.50.3"),sQuery(id+"F4.wireOp",EDGE,"E8.50.4"),sQuery(id+"F4.wireOp",EDGE,"E8.50.5")])]});
            var Q51;
            Q51=makeQuery(id+"F5.opExtrude","SWEPT_BODY",BODY,{"disambiguationData":[OSD([sQuery(id+"F4.wireOp",EDGE,"E8.51.0"),sQuery(id+"F4.wireOp",EDGE,"E8.51.1"),sQuery(id+"F4.wireOp",EDGE,"E8.51.2"),sQuery(id+"F4.wireOp",EDGE,"E8.51.3"),sQuery(id+"F4.wireOp",EDGE,"E8.51.4"),sQuery(id+"F4.wireOp",EDGE,"E8.51.5")])]});
            var Q52;
            Q52=makeQuery(id+"F5.opExtrude","SWEPT_BODY",BODY,{"disambiguationData":[OSD([sQuery(id+"F4.wireOp",EDGE,"E8.52.0"),sQuery(id+"F4.wireOp",EDGE,"E8.52.1"),sQuery(id+"F4.wireOp",EDGE,"E8.52.2"),sQuery(id+"F4.wireOp",EDGE,"E8.52.3"),sQuery(id+"F4.wireOp",EDGE,"E8.52.4"),sQuery(id+"F4.wireOp",EDGE,"E8.52.5")])]});
            var Q53;
            Q53=makeQuery(id+"F5.opExtrude","SWEPT_BODY",BODY,{"disambiguationData":[OSD([sQuery(id+"F4.wireOp",EDGE,"E8.53.0"),sQuery(id+"F4.wireOp",EDGE,"E8.53.1"),sQuery(id+"F4.wireOp",EDGE,"E8.53.2"),sQuery(id+"F4.wireOp",EDGE,"E8.53.3"),sQuery(id+"F4.wireOp",EDGE,"E8.53.4"),sQuery(id+"F4.wireOp",EDGE,"E8.53.5")])]});
            var Q54;
            Q54=makeQuery(id+"F5.opExtrude","SWEPT_BODY",BODY,{"disambiguationData":[OSD([sQuery(id+"F4.wireOp",EDGE,"E8.54.0"),sQuery(id+"F4.wireOp",EDGE,"E8.54.1"),sQuery(id+"F4.wireOp",EDGE,"E8.54.2"),sQuery(id+"F4.wireOp",EDGE,"E8.54.3"),sQuery(id+"F4.wireOp",EDGE,"E8.54.4"),sQuery(id+"F4.wireOp",EDGE,"E8.54.5")])]});
            var Q55;
            Q55=makeQuery(id+"F5.opExtrude","SWEPT_BODY",BODY,{"disambiguationData":[OSD([sQuery(id+"F4.wireOp",EDGE,"E8.55.0"),sQuery(id+"F4.wireOp",EDGE,"E8.55.1"),sQuery(id+"F4.wireOp",EDGE,"E8.55.2"),sQuery(id+"F4.wireOp",EDGE,"E8.55.3"),sQuery(id+"F4.wireOp",EDGE,"E8.55.4"),sQuery(id+"F4.wireOp",EDGE,"E8.55.5")])]});
            var Q56;
            Q56=makeQuery(id+"F5.opExtrude","SWEPT_BODY",BODY,{"disambiguationData":[OSD([sQuery(id+"F4.wireOp",EDGE,"E8.56.0"),sQuery(id+"F4.wireOp",EDGE,"E8.56.1"),sQuery(id+"F4.wireOp",EDGE,"E8.56.2"),sQuery(id+"F4.wireOp",EDGE,"E8.56.3"),sQuery(id+"F4.wireOp",EDGE,"E8.56.4"),sQuery(id+"F4.wireOp",EDGE,"E8.56.5")])]});
            var Q57;
            Q57=makeQuery(id+"F5.opExtrude","SWEPT_BODY",BODY,{"disambiguationData":[OSD([sQuery(id+"F4.wireOp",EDGE,"E8.57.0"),sQuery(id+"F4.wireOp",EDGE,"E8.57.1"),sQuery(id+"F4.wireOp",EDGE,"E8.57.2"),sQuery(id+"F4.wireOp",EDGE,"E8.57.3"),sQuery(id+"F4.wireOp",EDGE,"E8.57.4"),sQuery(id+"F4.wireOp",EDGE,"E8.57.5")])]});
            var Q58;
            Q58=makeQuery(id+"F5.opExtrude","SWEPT_BODY",BODY,{"disambiguationData":[OSD([sQuery(id+"F4.wireOp",EDGE,"E8.58.0"),sQuery(id+"F4.wireOp",EDGE,"E8.58.1"),sQuery(id+"F4.wireOp",EDGE,"E8.58.2"),sQuery(id+"F4.wireOp",EDGE,"E8.58.3"),sQuery(id+"F4.wireOp",EDGE,"E8.58.4"),sQuery(id+"F4.wireOp",EDGE,"E8.58.5")])]});
            var Q59;
            Q59=makeQuery(id+"F5.opExtrude","SWEPT_BODY",BODY,{"disambiguationData":[OSD([sQuery(id+"F4.wireOp",EDGE,"E8.59.0"),sQuery(id+"F4.wireOp",EDGE,"E8.59.1"),sQuery(id+"F4.wireOp",EDGE,"E8.59.2"),sQuery(id+"F4.wireOp",EDGE,"E8.59.3"),sQuery(id+"F4.wireOp",EDGE,"E8.59.4"),sQuery(id+"F4.wireOp",EDGE,"E8.59.5")])]});
            var Q60;
            Q60=makeQuery(id+"F1.opExtrude","SWEPT_BODY",BODY,{"disambiguationData":[OSD([sQuery(id+"F0.wireOp",EDGE,"E0"),sQuery(id+"F0.wireOp",EDGE,"E1")])]});
            booleanBodies(context, id + "F7", {"operationType" : BooleanOperationType.SUBTRACTION, "tools" : qUnion([Q0, Q1, Q2, Q3, Q4, Q5, Q6, Q7, Q8, Q9, Q10, Q11, Q12, Q13, Q14, Q15, Q16, Q17, Q18, Q19, Q20, Q21, Q22, Q23, Q24, Q25, Q26, Q27, Q28, Q29, Q30, Q31, Q32, Q33, Q34, Q35, Q36, Q37, Q38, Q39, Q40, Q41, Q42, Q43, Q44, Q45, Q46, Q47, Q48, Q49, Q50, Q51, Q52, Q53, Q54, Q55, Q56, Q57, Q58, Q59]), "targets" : qUnion([Q60])});
        }
        {
            var Q0;
            Q0=makeQuery(id+"F1.opExtrude","CAP_FACE",FACE,{"disambiguationData":[OSD([sQuery(id+"F0.wireOp",EDGE,"E0"),sQuery(id+"F0.wireOp",EDGE,"E1")])],"isStart":true});
            var sketch = newSketch(context, id + "F8", { "sketchPlane" : qUnion([Q0])});
            skCircle(sketch, "E9", {"center": v(-10, 0) * mm, "radius": 1.5 * mm});
            skCircle(sketch, "E10.MirrorC", {"center": v(10, 0) * mm, "radius": 1.5 * mm});
            skSolve(sketch);
        }
        {
            var Q0;
            Q0=makeQuery(id+"F8.imprint","IMPRINT",FACE,{"disambiguationData":[TD([[makeQuery(id+"F8.imprint","IMPRINT",EDGE,{"derivedFrom":sQuery(id+"F8.wireOp",EDGE,"E9")}),1.0]])]});
            var Q1;
            Q1=makeQuery(id+"F8.imprint","IMPRINT",FACE,{"disambiguationData":[TD([[makeQuery(id+"F8.imprint","IMPRINT",EDGE,{"derivedFrom":sQuery(id+"F8.wireOp",EDGE,"E10.MirrorC")}),-1.0]])]});
            extrude(context, id + "F9", {"entities" : qUnion([Q0, Q1]), "operationType" : NewBodyOperationType.REMOVE, "oppositeDirection" : true, "depth" : 1.5 * mm});
        }
        {
            var Q0;
            Q0=makeQuery(id+"F1.opExtrude","SWEPT_BODY",BODY,{"disambiguationData":[OSD([sQuery(id+"F0.wireOp",EDGE,"E0"),sQuery(id+"F0.wireOp",EDGE,"E1")])]});
            var Q1;
            Q1=makeQuery(id+"F1.opExtrude","CAP_FACE",FACE,{"disambiguationData":[OSD([sQuery(id+"F0.wireOp",EDGE,"E0"),sQuery(id+"F0.wireOp",EDGE,"E1")])],"isStart":true});
            mirror(context, id + "F10", {"entities" : qUnion([Q0]), "mirrorPlane" : qUnion([Q1])});
        }
    });
